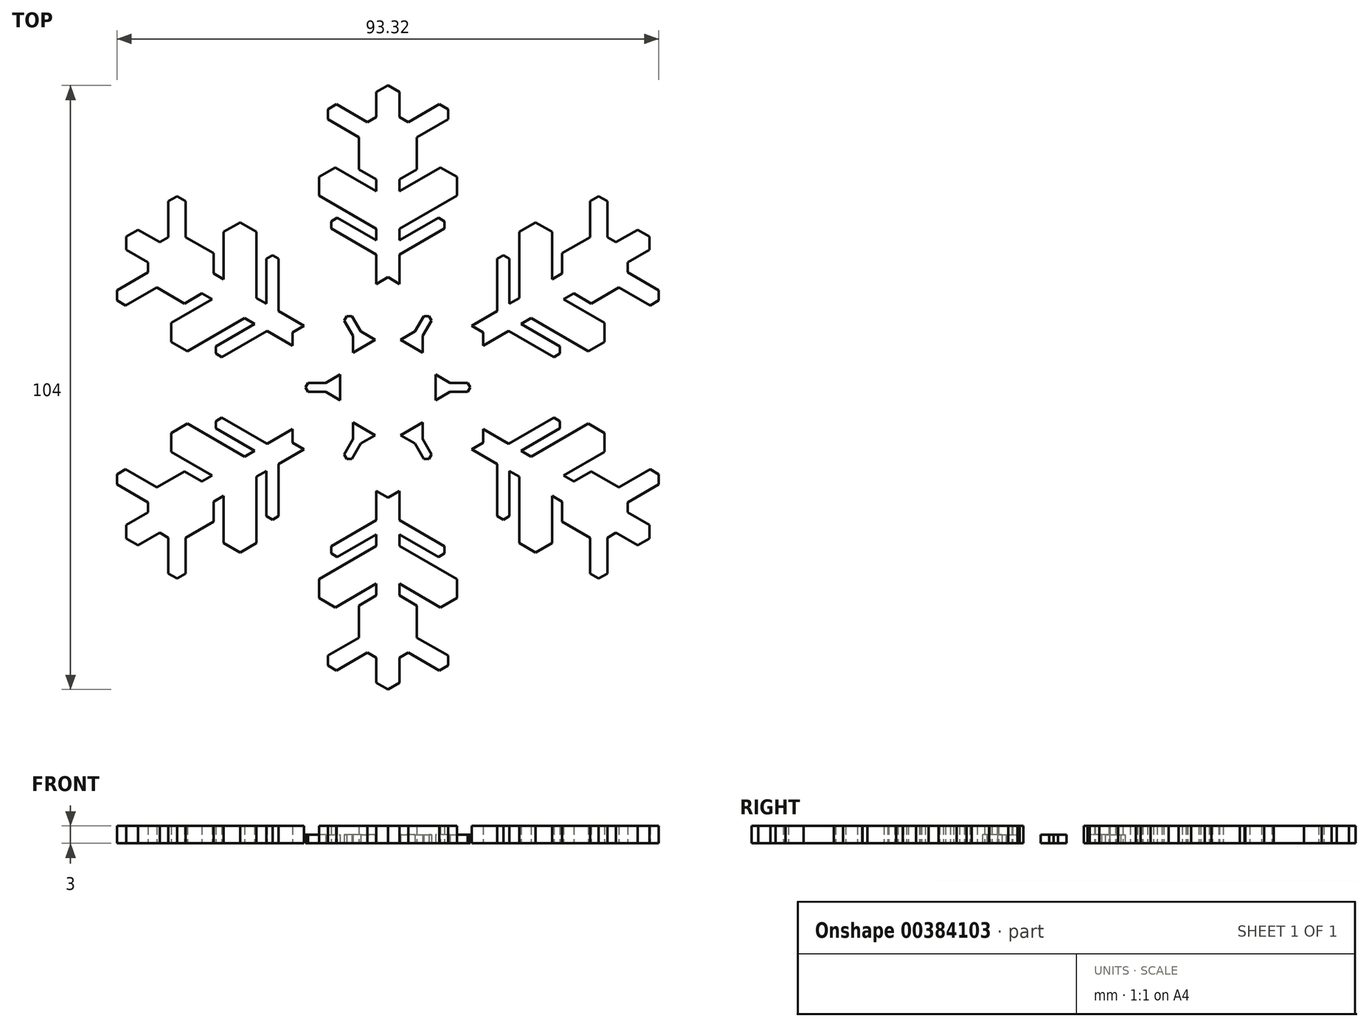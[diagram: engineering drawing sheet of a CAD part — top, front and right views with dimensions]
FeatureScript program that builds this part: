
annotation { "Feature Type Name" : "Feature", "Feature Type Description" : "" }
export const myFeature = defineFeature(function(context is Context, id is Id, definition is map)
    precondition{}
    {
        {
            var Q0;
            Q0=qCreatedBy(makeId("Top.planeOp"),FACE);
            var sketch = newSketch(context, id + "F0", { "sketchPlane" : qUnion([Q0])});
            skLineSegment(sketch, "E0", {"start": v(0, 26) * mm, "end": v(0, -26) * mm, "construction": true});
            skLineSegment(sketch, "E1", {"start": v(22.52, -13) * mm, "end": v(-22.52, 13) * mm, "construction": true});
            skLineSegment(sketch, "E2", {"start": v(22.52, 13) * mm, "end": v(-22.52, -13) * mm, "construction": true});
            skLineSegment(sketch, "E3", {"start": v(0, 9.48) * mm, "end": v(-8.21, 4.74) * mm});
            skLineSegment(sketch, "E4", {"start": v(0, 0) * mm, "end": v(-4.1, 7.11) * mm, "construction": true});
            skLineSegment(sketch, "E5", {"start": v(0, 0) * mm, "end": v(-3.22, 7.62) * mm});
            skLineSegment(sketch, "E6", {"start": v(0, 0) * mm, "end": v(-5, 6.6) * mm});
            skLineSegment(sketch, "E7", {"start": v(0, 2.4) * mm, "end": v(-2.08, 1.2) * mm});
            skLineSegment(sketch, "E8", {"start": v(-1, 8.9) * mm, "end": v(-1, 25.42) * mm});
            skLineSegment(sketch, "E9", {"start": v(-1, 25.42) * mm, "end": v(0, 26) * mm});
            skLineSegment(sketch, "E10", {"start": v(-1, 23.27) * mm, "end": v(-2.5, 22.4) * mm});
            skLineSegment(sketch, "E11", {"start": v(-2.5, 22.4) * mm, "end": v(-2.5, 18.78) * mm});
            skLineSegment(sketch, "E12", {"start": v(-2.5, 18.78) * mm, "end": v(-1, 17.91) * mm});
            skLineSegment(sketch, "E13", {"start": v(-1.75, 22.84) * mm, "end": v(-4.43, 24.38) * mm});
            skLineSegment(sketch, "E14", {"start": v(-4.43, 24.38) * mm, "end": v(-5.18, 23.95) * mm});
            skLineSegment(sketch, "E15", {"start": v(-5.18, 23.95) * mm, "end": v(-5.18, 23.08) * mm});
            skLineSegment(sketch, "E16", {"start": v(-5.18, 23.08) * mm, "end": v(-2.5, 21.54) * mm});
            skLineSegment(sketch, "E17", {"start": v(-5.18, 23.08) * mm, "end": v(-4.43, 24.38) * mm, "construction": true});
            skLineSegment(sketch, "E18", {"start": v(-5.18, 23.95) * mm, "end": v(-4.8, 23.73) * mm, "construction": true});
            skLineSegment(sketch, "E19", {"start": v(-4.8, 23.73) * mm, "end": v(-2.5, 22.4) * mm, "construction": true});
            skLineSegment(sketch, "E20", {"start": v(-1, 16.9) * mm, "end": v(-4.53, 18.94) * mm});
            skLineSegment(sketch, "E21", {"start": v(-4.53, 18.94) * mm, "end": v(-5.94, 18.13) * mm});
            skLineSegment(sketch, "E22", {"start": v(-5.94, 18.13) * mm, "end": v(-5.94, 16.5) * mm});
            skLineSegment(sketch, "E23", {"start": v(-5.94, 16.5) * mm, "end": v(-1, 13.65) * mm});
            skLineSegment(sketch, "E24", {"start": v(-5.94, 16.5) * mm, "end": v(-4.53, 18.94) * mm, "construction": true});
            skLineSegment(sketch, "E25", {"start": v(-5.94, 18.13) * mm, "end": v(-5.23, 17.72) * mm, "construction": true});
            skPoint(sketch, "E25.endSnap0", {"position": v(-5.23, 17.72) * mm});
            skLineSegment(sketch, "E26", {"start": v(-1, 12.67) * mm, "end": v(-4.35, 14.6) * mm});
            skLineSegment(sketch, "E27", {"start": v(-4.35, 14.6) * mm, "end": v(-4.89, 14.3) * mm});
            skLineSegment(sketch, "E28", {"start": v(-4.89, 14.3) * mm, "end": v(-4.89, 13.68) * mm});
            skLineSegment(sketch, "E29", {"start": v(-4.89, 13.68) * mm, "end": v(-1, 11.44) * mm});
            skLineSegment(sketch, "E30", {"start": v(-4.89, 13.68) * mm, "end": v(-4.35, 14.6) * mm, "construction": true});
            skLineSegment(sketch, "E31", {"start": v(-4.89, 14.3) * mm, "end": v(-4.62, 14.14) * mm, "construction": true});
            skLineSegment(sketch, "E32", {"start": v(-4.1, 7.11) * mm, "end": v(-15.85, 27.45) * mm, "construction": true});
            skLineSegment(sketch, "E33", {"start": v(-6.02, 10.43) * mm, "end": v(-2.2, 8.22) * mm});
            skLineSegment(sketch, "E34", {"start": v(-4.69, 9.66) * mm, "end": v(-6.2, 12.29) * mm});
            skLineSegment(sketch, "E35", {"start": v(-6.2, 12.29) * mm, "end": v(-7.1, 12.29) * mm});
            skLineSegment(sketch, "E36", {"start": v(-7.21, 4.16) * mm, "end": v(0, 8.33) * mm});
            skLineSegment(sketch, "E37.MirrorCS", {"start": v(5.18, 23.95) * mm, "end": v(4.8, 23.73) * mm, "construction": true});
            skLineSegment(sketch, "E38.MirrorCS", {"start": v(4.89, 14.3) * mm, "end": v(4.62, 14.14) * mm, "construction": true});
            skLineSegment(sketch, "E39.MirrorCS", {"start": v(4.43, 24.38) * mm, "end": v(5.18, 23.95) * mm});
            skLineSegment(sketch, "E40.MirrorCS", {"start": v(5.18, 23.95) * mm, "end": v(5.18, 23.08) * mm});
            skLineSegment(sketch, "E41.MirrorCS", {"start": v(5.94, 18.13) * mm, "end": v(5.94, 16.5) * mm});
            skLineSegment(sketch, "E42.MirrorCS", {"start": v(5.94, 18.13) * mm, "end": v(5.23, 17.72) * mm, "construction": true});
            skLineSegment(sketch, "E43.MirrorCS", {"start": v(4.89, 14.3) * mm, "end": v(4.89, 13.68) * mm});
            skLineSegment(sketch, "E44.MirrorCS", {"start": v(4.53, 18.94) * mm, "end": v(5.94, 18.13) * mm});
            skLineSegment(sketch, "E45.MirrorCS", {"start": v(4.89, 13.68) * mm, "end": v(4.35, 14.6) * mm, "construction": true});
            skLineSegment(sketch, "E46.MirrorCS", {"start": v(5.18, 23.08) * mm, "end": v(4.43, 24.38) * mm, "construction": true});
            skLineSegment(sketch, "E47.MirrorCS", {"start": v(4.35, 14.6) * mm, "end": v(4.89, 14.3) * mm});
            skLineSegment(sketch, "E48.MirrorCS", {"start": v(5.94, 16.5) * mm, "end": v(4.53, 18.94) * mm, "construction": true});
            skLineSegment(sketch, "E49.MirrorCS", {"start": v(1, 25.42) * mm, "end": v(0, 26) * mm});
            skLineSegment(sketch, "E50.MirrorCS", {"start": v(6.2, 12.29) * mm, "end": v(7.1, 12.29) * mm});
            skLineSegment(sketch, "E51.MirrorCS", {"start": v(1.75, 22.84) * mm, "end": v(4.43, 24.38) * mm});
            skLineSegment(sketch, "E52.MirrorCS", {"start": v(1, 23.27) * mm, "end": v(2.5, 22.4) * mm});
            skLineSegment(sketch, "E53.MirrorCS", {"start": v(1, 12.67) * mm, "end": v(4.35, 14.6) * mm});
            skLineSegment(sketch, "E54.MirrorCS", {"start": v(2.5, 18.78) * mm, "end": v(1, 17.91) * mm});
            skLineSegment(sketch, "E55.MirrorCS", {"start": v(4.69, 9.66) * mm, "end": v(6.2, 12.29) * mm});
            skPoint(sketch, "E56.MirrorP", {"position": v(5.23, 17.72) * mm});
            skLineSegment(sketch, "E57.MirrorCS", {"start": v(5.18, 23.08) * mm, "end": v(2.5, 21.54) * mm});
            skLineSegment(sketch, "E58.MirrorCS", {"start": v(4.89, 13.68) * mm, "end": v(1, 11.44) * mm});
            skLineSegment(sketch, "E59.MirrorCS", {"start": v(7.21, 4.16) * mm, "end": v(0, 8.33) * mm});
            skLineSegment(sketch, "E60.MirrorCS", {"start": v(5.94, 16.5) * mm, "end": v(1, 13.65) * mm});
            skLineSegment(sketch, "E61.MirrorCS", {"start": v(1, 16.9) * mm, "end": v(4.53, 18.94) * mm});
            skLineSegment(sketch, "E62.MirrorCS", {"start": v(2.5, 22.4) * mm, "end": v(2.5, 18.78) * mm});
            skLineSegment(sketch, "E63.MirrorCS", {"start": v(0, 9.48) * mm, "end": v(8.21, 4.74) * mm});
            skLineSegment(sketch, "E64.MirrorCS", {"start": v(0, 0) * mm, "end": v(4.1, 7.11) * mm, "construction": true});
            skLineSegment(sketch, "E65.MirrorCS", {"start": v(4.8, 23.73) * mm, "end": v(2.5, 22.4) * mm, "construction": true});
            skLineSegment(sketch, "E66.MirrorCS", {"start": v(6.02, 10.43) * mm, "end": v(2.2, 8.22) * mm});
            skLineSegment(sketch, "E67.MirrorCS", {"start": v(0, 0) * mm, "end": v(5, 6.6) * mm});
            skLineSegment(sketch, "E68.MirrorCS", {"start": v(0, 0) * mm, "end": v(3.22, 7.62) * mm});
            skLineSegment(sketch, "E69.MirrorCS", {"start": v(1, 8.9) * mm, "end": v(1, 25.42) * mm});
            skLineSegment(sketch, "E70.MirrorCS", {"start": v(0, 2.4) * mm, "end": v(2.08, 1.2) * mm});
            skLineSegment(sketch, "E71.1.0", {"start": v(0, 8.33) * mm, "end": v(-7.21, 4.16) * mm});
            skLineSegment(sketch, "E71.1.1", {"start": v(-15.14, 7.58) * mm, "end": v(-18.67, 5.55) * mm});
            skLineSegment(sketch, "E71.1.2", {"start": v(-7.21, 5.32) * mm, "end": v(-21.52, 13.58) * mm});
            skLineSegment(sketch, "E71.1.3", {"start": v(-18.15, 13.37) * mm, "end": v(-15.01, 11.56) * mm});
            skLineSegment(sketch, "E71.1.4", {"start": v(-14.29, 2.6) * mm, "end": v(-10.4, 4.85) * mm});
            skPoint(sketch, "E71.1.5", {"position": v(-12.73, 13.4) * mm});
            skLineSegment(sketch, "E71.1.6", {"start": v(-22.95, 7.7) * mm, "end": v(-20.65, 9.04) * mm, "construction": true});
            skLineSegment(sketch, "E71.1.7", {"start": v(-11.32, 13.4) * mm, "end": v(-11.32, 7.7) * mm});
            skLineSegment(sketch, "E71.1.8", {"start": v(-7.21, -4.16) * mm, "end": v(-7.21, 4.16) * mm});
            skLineSegment(sketch, "E71.1.9", {"start": v(-14.14, 9.32) * mm, "end": v(-14.14, 13.4) * mm});
            skLineSegment(sketch, "E71.1.11", {"start": v(-2.08, 1.2) * mm, "end": v(0, 2.4) * mm});
            skLineSegment(sketch, "E71.1.13", {"start": v(-8.21, 4.74) * mm, "end": v(0, 9.48) * mm});
            skLineSegment(sketch, "E71.1.14", {"start": v(-18.9, 12.93) * mm, "end": v(-18.9, 16.02) * mm});
            skPoint(sketch, "E71.1.15", {"position": v(-17.96, 4.33) * mm});
            skLineSegment(sketch, "E71.1.16", {"start": v(-15.01, 11.56) * mm, "end": v(-15.01, 9.82) * mm});
            skLineSegment(sketch, "E71.1.17", {"start": v(-8.21, 4.74) * mm, "end": v(-8.21, -4.74) * mm});
            skLineSegment(sketch, "E71.1.18", {"start": v(0, 0) * mm, "end": v(-8.21, 0) * mm, "construction": true});
            skLineSegment(sketch, "E71.1.19", {"start": v(0, 0) * mm, "end": v(-8.21, 1.02) * mm});
            skLineSegment(sketch, "E71.1.20", {"start": v(0, 0) * mm, "end": v(-8.21, -1.02) * mm});
            skLineSegment(sketch, "E71.1.21", {"start": v(-2.08, 1.2) * mm, "end": v(-2.08, -1.2) * mm});
            skLineSegment(sketch, "E71.1.22", {"start": v(-8.21, 3.59) * mm, "end": v(-22.52, 11.85) * mm});
            skLineSegment(sketch, "E71.1.23", {"start": v(-20.65, 9.04) * mm, "end": v(-17.51, 7.23) * mm});
            skLineSegment(sketch, "E71.1.24", {"start": v(-17.51, 7.23) * mm, "end": v(-16.01, 8.1) * mm});
            skLineSegment(sketch, "E71.1.25", {"start": v(-6.02, 8.89) * mm, "end": v(-7.54, 11.52) * mm});
            skLineSegment(sketch, "E71.1.26", {"start": v(-17.26, 3.1) * mm, "end": v(-12.32, 5.96) * mm});
            skLineSegment(sketch, "E71.1.27", {"start": v(-22.58, 7.06) * mm, "end": v(-19.9, 8.6) * mm});
            skLineSegment(sketch, "E71.1.28", {"start": v(-18.15, 16.02) * mm, "end": v(-18.15, 13.37) * mm, "construction": true});
            skLineSegment(sketch, "E71.1.29", {"start": v(-17.4, 16.02) * mm, "end": v(-17.4, 12.93) * mm});
            skLineSegment(sketch, "E71.1.30", {"start": v(-6.02, 10.43) * mm, "end": v(-6.02, 6) * mm});
            skLineSegment(sketch, "E71.1.31", {"start": v(-12.04, 0) * mm, "end": v(-8.21, 2.2) * mm});
            skLineSegment(sketch, "E71.1.32", {"start": v(-9.4, 11.07) * mm, "end": v(-9.4, 6.58) * mm});
            skLineSegment(sketch, "E71.1.34", {"start": v(-10.7, 0.77) * mm, "end": v(-13.75, 0.77) * mm});
            skLineSegment(sketch, "E71.1.35", {"start": v(-19.65, 12.5) * mm, "end": v(-18.15, 13.37) * mm});
            skLineSegment(sketch, "E71.1.36", {"start": v(-20.65, 9.9) * mm, "end": v(-23.33, 8.36) * mm});
            skLineSegment(sketch, "E71.1.37", {"start": v(-10.47, 7.2) * mm, "end": v(-10.47, 11.07) * mm});
            skLineSegment(sketch, "E71.1.38", {"start": v(-13.75, 0.77) * mm, "end": v(-14.2, 0) * mm});
            skLineSegment(sketch, "E71.1.39", {"start": v(-20.65, 10.77) * mm, "end": v(-20.65, 9.04) * mm});
            skLineSegment(sketch, "E71.1.40", {"start": v(-7.54, 11.52) * mm, "end": v(-7.1, 12.29) * mm});
            skLineSegment(sketch, "E71.1.41", {"start": v(-11.47, 5.47) * mm, "end": v(-14.82, 3.53) * mm});
            skLineSegment(sketch, "E71.1.42", {"start": v(-22.52, 11.85) * mm, "end": v(-22.52, 13) * mm});
            skLineSegment(sketch, "E71.1.43", {"start": v(-11.32, 13.4) * mm, "end": v(-14.14, 13.4) * mm, "construction": true});
            skLineSegment(sketch, "E71.1.44", {"start": v(-17.26, 3.1) * mm, "end": v(-18.67, 5.55) * mm, "construction": true});
            skLineSegment(sketch, "E71.1.45", {"start": v(-21.52, 13.58) * mm, "end": v(-22.52, 13) * mm});
            skLineSegment(sketch, "E71.1.46", {"start": v(-9.94, 11.38) * mm, "end": v(-9.4, 11.07) * mm});
            skLineSegment(sketch, "E71.1.47", {"start": v(-12.73, 14.2) * mm, "end": v(-12.73, 13.4) * mm, "construction": true});
            skLineSegment(sketch, "E71.1.48", {"start": v(-23.33, 8.36) * mm, "end": v(-23.33, 7.5) * mm});
            skLineSegment(sketch, "E71.1.49", {"start": v(-9.4, 11.07) * mm, "end": v(-10.47, 11.07) * mm, "construction": true});
            skLineSegment(sketch, "E71.1.50", {"start": v(-14.82, 2.92) * mm, "end": v(-14.56, 3.07) * mm, "construction": true});
            skLineSegment(sketch, "E71.1.51", {"start": v(-14.82, 3.53) * mm, "end": v(-14.82, 2.92) * mm});
            skLineSegment(sketch, "E71.1.52", {"start": v(-14.82, 2.92) * mm, "end": v(-14.29, 2.6) * mm});
            skLineSegment(sketch, "E71.1.53", {"start": v(-14.14, 13.4) * mm, "end": v(-12.73, 14.2) * mm});
            skLineSegment(sketch, "E71.1.54", {"start": v(-18.67, 5.55) * mm, "end": v(-18.67, 3.92) * mm});
            skLineSegment(sketch, "E71.1.55", {"start": v(-18.67, 3.92) * mm, "end": v(-17.26, 3.1) * mm});
            skLineSegment(sketch, "E71.1.56", {"start": v(-9.94, 11.38) * mm, "end": v(-9.94, 11.07) * mm, "construction": true});
            skLineSegment(sketch, "E71.1.57", {"start": v(-18.15, 16.46) * mm, "end": v(-18.15, 16.02) * mm, "construction": true});
            skLineSegment(sketch, "E71.1.58", {"start": v(-17.4, 16.02) * mm, "end": v(-18.9, 16.02) * mm, "construction": true});
            skLineSegment(sketch, "E71.1.59", {"start": v(-23.33, 7.5) * mm, "end": v(-22.58, 7.06) * mm});
            skLineSegment(sketch, "E71.1.60", {"start": v(-14.29, 2.6) * mm, "end": v(-14.82, 3.53) * mm, "construction": true});
            skLineSegment(sketch, "E71.1.61", {"start": v(-10.47, 11.07) * mm, "end": v(-9.94, 11.38) * mm});
            skLineSegment(sketch, "E71.1.62", {"start": v(-18.9, 16.02) * mm, "end": v(-18.15, 16.46) * mm});
            skLineSegment(sketch, "E71.1.63", {"start": v(-18.15, 16.46) * mm, "end": v(-17.4, 16.02) * mm});
            skLineSegment(sketch, "E71.1.64", {"start": v(-22.58, 7.06) * mm, "end": v(-23.33, 8.36) * mm, "construction": true});
            skLineSegment(sketch, "E71.1.65", {"start": v(-12.73, 14.2) * mm, "end": v(-11.32, 13.4) * mm});
            skLineSegment(sketch, "E71.1.66", {"start": v(-18.67, 3.92) * mm, "end": v(-17.96, 4.33) * mm, "construction": true});
            skLineSegment(sketch, "E71.1.67", {"start": v(-23.33, 7.5) * mm, "end": v(-22.95, 7.7) * mm, "construction": true});
            skLineSegment(sketch, "E71.2.0", {"start": v(-7.21, 4.16) * mm, "end": v(-7.21, -4.16) * mm});
            skLineSegment(sketch, "E71.2.1", {"start": v(-14.14, -9.32) * mm, "end": v(-14.14, -13.4) * mm});
            skLineSegment(sketch, "E71.2.2", {"start": v(-8.21, -3.59) * mm, "end": v(-22.52, -11.85) * mm});
            skLineSegment(sketch, "E71.2.3", {"start": v(-20.65, -9.04) * mm, "end": v(-17.51, -7.23) * mm});
            skLineSegment(sketch, "E71.2.4", {"start": v(-9.4, -11.07) * mm, "end": v(-9.4, -6.58) * mm});
            skPoint(sketch, "E71.2.5", {"position": v(-17.96, -4.33) * mm});
            skLineSegment(sketch, "E71.2.6", {"start": v(-18.15, -16.02) * mm, "end": v(-18.15, -13.37) * mm, "construction": true});
            skLineSegment(sketch, "E71.2.7", {"start": v(-17.26, -3.1) * mm, "end": v(-12.32, -5.96) * mm});
            skLineSegment(sketch, "E71.2.8", {"start": v(0, -8.33) * mm, "end": v(-7.21, -4.16) * mm});
            skLineSegment(sketch, "E71.2.9", {"start": v(-15.14, -7.58) * mm, "end": v(-18.67, -5.55) * mm});
            skLineSegment(sketch, "E71.2.10", {"start": v(0, 0) * mm, "end": v(-8.21, -1.02) * mm});
            skLineSegment(sketch, "E71.2.11", {"start": v(-2.08, -1.2) * mm, "end": v(-2.08, 1.2) * mm});
            skLineSegment(sketch, "E71.2.12", {"start": v(0, 0) * mm, "end": v(-8.21, 0) * mm, "construction": true});
            skLineSegment(sketch, "E71.2.13", {"start": v(-8.21, -4.74) * mm, "end": v(-8.21, 4.74) * mm});
            skLineSegment(sketch, "E71.2.14", {"start": v(-20.65, -9.9) * mm, "end": v(-23.33, -8.36) * mm});
            skPoint(sketch, "E71.2.15", {"position": v(-12.73, -13.4) * mm});
            skLineSegment(sketch, "E71.2.16", {"start": v(-17.51, -7.23) * mm, "end": v(-16.01, -8.1) * mm});
            skLineSegment(sketch, "E71.2.17", {"start": v(-8.21, -4.74) * mm, "end": v(0, -9.48) * mm});
            skLineSegment(sketch, "E71.2.18", {"start": v(0, 0) * mm, "end": v(-4.1, -7.11) * mm, "construction": true});
            skLineSegment(sketch, "E71.2.19", {"start": v(0, 0) * mm, "end": v(-5, -6.6) * mm});
            skLineSegment(sketch, "E71.2.20", {"start": v(0, 0) * mm, "end": v(-3.22, -7.62) * mm});
            skLineSegment(sketch, "E71.2.21", {"start": v(-2.08, -1.2) * mm, "end": v(0, -2.4) * mm});
            skLineSegment(sketch, "E71.2.22", {"start": v(-7.21, -5.32) * mm, "end": v(-21.52, -13.58) * mm});
            skLineSegment(sketch, "E71.2.23", {"start": v(-18.15, -13.37) * mm, "end": v(-15.01, -11.56) * mm});
            skLineSegment(sketch, "E71.2.24", {"start": v(-15.01, -11.56) * mm, "end": v(-15.01, -9.82) * mm});
            skLineSegment(sketch, "E71.2.25", {"start": v(-10.7, -0.77) * mm, "end": v(-13.75, -0.77) * mm});
            skLineSegment(sketch, "E71.2.26", {"start": v(-11.32, -13.4) * mm, "end": v(-11.32, -7.7) * mm});
            skLineSegment(sketch, "E71.2.27", {"start": v(-17.4, -16.02) * mm, "end": v(-17.4, -12.93) * mm});
            skLineSegment(sketch, "E71.2.28", {"start": v(-22.95, -7.7) * mm, "end": v(-20.65, -9.04) * mm, "construction": true});
            skLineSegment(sketch, "E71.2.29", {"start": v(-22.58, -7.06) * mm, "end": v(-19.9, -8.6) * mm});
            skLineSegment(sketch, "E71.2.30", {"start": v(-12.04, 0) * mm, "end": v(-8.21, -2.2) * mm});
            skLineSegment(sketch, "E71.2.31", {"start": v(-6.02, -10.43) * mm, "end": v(-6.02, -6) * mm});
            skLineSegment(sketch, "E71.2.32", {"start": v(-14.29, -2.6) * mm, "end": v(-10.4, -4.85) * mm});
            skLineSegment(sketch, "E71.2.33", {"start": v(0, 0) * mm, "end": v(-8.21, 1.02) * mm});
            skLineSegment(sketch, "E71.2.34", {"start": v(-6.02, -8.89) * mm, "end": v(-7.54, -11.52) * mm});
            skLineSegment(sketch, "E71.2.35", {"start": v(-20.65, -10.77) * mm, "end": v(-20.65, -9.04) * mm});
            skLineSegment(sketch, "E71.2.36", {"start": v(-18.9, -12.93) * mm, "end": v(-18.9, -16.02) * mm});
            skLineSegment(sketch, "E71.2.37", {"start": v(-11.47, -5.47) * mm, "end": v(-14.82, -3.53) * mm});
            skLineSegment(sketch, "E71.2.38", {"start": v(-7.54, -11.52) * mm, "end": v(-7.1, -12.29) * mm});
            skLineSegment(sketch, "E71.2.39", {"start": v(-19.65, -12.5) * mm, "end": v(-18.15, -13.37) * mm});
            skLineSegment(sketch, "E71.2.40", {"start": v(-13.75, -0.77) * mm, "end": v(-14.2, 0) * mm});
            skLineSegment(sketch, "E71.2.41", {"start": v(-10.47, -7.2) * mm, "end": v(-10.47, -11.07) * mm});
            skLineSegment(sketch, "E71.2.42", {"start": v(-21.52, -13.58) * mm, "end": v(-22.52, -13) * mm});
            skLineSegment(sketch, "E71.2.43", {"start": v(-17.26, -3.1) * mm, "end": v(-18.67, -5.55) * mm, "construction": true});
            skLineSegment(sketch, "E71.2.44", {"start": v(-11.32, -13.4) * mm, "end": v(-14.14, -13.4) * mm, "construction": true});
            skLineSegment(sketch, "E71.2.45", {"start": v(-22.52, -11.85) * mm, "end": v(-22.52, -13) * mm});
            skLineSegment(sketch, "E71.2.46", {"start": v(-14.82, -2.92) * mm, "end": v(-14.29, -2.6) * mm});
            skLineSegment(sketch, "E71.2.47", {"start": v(-18.67, -3.92) * mm, "end": v(-17.96, -4.33) * mm, "construction": true});
            skLineSegment(sketch, "E71.2.48", {"start": v(-18.9, -16.02) * mm, "end": v(-18.15, -16.46) * mm});
            skLineSegment(sketch, "E71.2.49", {"start": v(-14.29, -2.6) * mm, "end": v(-14.82, -3.53) * mm, "construction": true});
            skLineSegment(sketch, "E71.2.50", {"start": v(-9.94, -11.38) * mm, "end": v(-9.94, -11.07) * mm, "construction": true});
            skLineSegment(sketch, "E71.2.51", {"start": v(-10.47, -11.07) * mm, "end": v(-9.94, -11.38) * mm});
            skLineSegment(sketch, "E71.2.52", {"start": v(-9.94, -11.38) * mm, "end": v(-9.4, -11.07) * mm});
            skLineSegment(sketch, "E71.2.53", {"start": v(-18.67, -5.55) * mm, "end": v(-18.67, -3.92) * mm});
            skLineSegment(sketch, "E71.2.54", {"start": v(-14.14, -13.4) * mm, "end": v(-12.73, -14.2) * mm});
            skLineSegment(sketch, "E71.2.55", {"start": v(-12.73, -14.2) * mm, "end": v(-11.32, -13.4) * mm});
            skLineSegment(sketch, "E71.2.56", {"start": v(-14.82, -2.92) * mm, "end": v(-14.56, -3.07) * mm, "construction": true});
            skLineSegment(sketch, "E71.2.57", {"start": v(-23.33, -7.5) * mm, "end": v(-22.95, -7.7) * mm, "construction": true});
            skLineSegment(sketch, "E71.2.58", {"start": v(-22.58, -7.06) * mm, "end": v(-23.33, -8.36) * mm, "construction": true});
            skLineSegment(sketch, "E71.2.59", {"start": v(-18.15, -16.46) * mm, "end": v(-17.4, -16.02) * mm});
            skLineSegment(sketch, "E71.2.60", {"start": v(-9.4, -11.07) * mm, "end": v(-10.47, -11.07) * mm, "construction": true});
            skLineSegment(sketch, "E71.2.61", {"start": v(-14.82, -3.53) * mm, "end": v(-14.82, -2.92) * mm});
            skLineSegment(sketch, "E71.2.62", {"start": v(-23.33, -8.36) * mm, "end": v(-23.33, -7.5) * mm});
            skLineSegment(sketch, "E71.2.63", {"start": v(-23.33, -7.5) * mm, "end": v(-22.58, -7.06) * mm});
            skLineSegment(sketch, "E71.2.64", {"start": v(-17.4, -16.02) * mm, "end": v(-18.9, -16.02) * mm, "construction": true});
            skLineSegment(sketch, "E71.2.65", {"start": v(-18.67, -3.92) * mm, "end": v(-17.26, -3.1) * mm});
            skLineSegment(sketch, "E71.2.66", {"start": v(-12.73, -14.2) * mm, "end": v(-12.73, -13.4) * mm, "construction": true});
            skLineSegment(sketch, "E71.2.67", {"start": v(-18.15, -16.46) * mm, "end": v(-18.15, -16.02) * mm, "construction": true});
            skLineSegment(sketch, "E71.3.0", {"start": v(-7.21, -4.16) * mm, "end": v(0, -8.33) * mm});
            skLineSegment(sketch, "E71.3.1", {"start": v(1, -16.9) * mm, "end": v(4.53, -18.94) * mm});
            skLineSegment(sketch, "E71.3.2", {"start": v(-1, -8.9) * mm, "end": v(-1, -25.42) * mm});
            skLineSegment(sketch, "E71.3.3", {"start": v(-2.5, -22.4) * mm, "end": v(-2.5, -18.78) * mm});
            skLineSegment(sketch, "E71.3.4", {"start": v(4.89, -13.68) * mm, "end": v(1, -11.44) * mm});
            skPoint(sketch, "E71.3.5", {"position": v(-5.23, -17.72) * mm});
            skLineSegment(sketch, "E71.3.6", {"start": v(4.8, -23.73) * mm, "end": v(2.5, -22.4) * mm, "construction": true});
            skLineSegment(sketch, "E71.3.7", {"start": v(-5.94, -16.5) * mm, "end": v(-1, -13.65) * mm});
            skLineSegment(sketch, "E71.3.8", {"start": v(7.21, -4.16) * mm, "end": v(0, -8.33) * mm});
            skLineSegment(sketch, "E71.3.9", {"start": v(-1, -16.9) * mm, "end": v(-4.53, -18.94) * mm});
            skLineSegment(sketch, "E71.3.10", {"start": v(0, 0) * mm, "end": v(-3.22, -7.62) * mm});
            skLineSegment(sketch, "E71.3.11", {"start": v(0, -2.4) * mm, "end": v(-2.08, -1.2) * mm});
            skLineSegment(sketch, "E71.3.12", {"start": v(0, 0) * mm, "end": v(-4.1, -7.11) * mm, "construction": true});
            skLineSegment(sketch, "E71.3.13", {"start": v(0, -9.48) * mm, "end": v(-8.21, -4.74) * mm});
            skLineSegment(sketch, "E71.3.14", {"start": v(-1.75, -22.84) * mm, "end": v(-4.43, -24.38) * mm});
            skPoint(sketch, "E71.3.15", {"position": v(5.23, -17.72) * mm});
            skLineSegment(sketch, "E71.3.16", {"start": v(-2.5, -18.78) * mm, "end": v(-1, -17.91) * mm});
            skLineSegment(sketch, "E71.3.17", {"start": v(0, -9.48) * mm, "end": v(8.21, -4.74) * mm});
            skLineSegment(sketch, "E71.3.18", {"start": v(0, 0) * mm, "end": v(4.1, -7.11) * mm, "construction": true});
            skLineSegment(sketch, "E71.3.19", {"start": v(0, 0) * mm, "end": v(3.22, -7.62) * mm});
            skLineSegment(sketch, "E71.3.20", {"start": v(0, 0) * mm, "end": v(5, -6.6) * mm});
            skLineSegment(sketch, "E71.3.21", {"start": v(0, -2.4) * mm, "end": v(2.08, -1.2) * mm});
            skLineSegment(sketch, "E71.3.22", {"start": v(1, -8.9) * mm, "end": v(1, -25.42) * mm});
            skLineSegment(sketch, "E71.3.23", {"start": v(2.5, -22.4) * mm, "end": v(2.5, -18.78) * mm});
            skLineSegment(sketch, "E71.3.24", {"start": v(2.5, -18.78) * mm, "end": v(1, -17.91) * mm});
            skLineSegment(sketch, "E71.3.25", {"start": v(-4.69, -9.66) * mm, "end": v(-6.2, -12.29) * mm});
            skLineSegment(sketch, "E71.3.26", {"start": v(5.94, -16.5) * mm, "end": v(1, -13.65) * mm});
            skLineSegment(sketch, "E71.3.27", {"start": v(5.18, -23.08) * mm, "end": v(2.5, -21.54) * mm});
            skLineSegment(sketch, "E71.3.28", {"start": v(-4.8, -23.73) * mm, "end": v(-2.5, -22.4) * mm, "construction": true});
            skLineSegment(sketch, "E71.3.29", {"start": v(-5.18, -23.08) * mm, "end": v(-2.5, -21.54) * mm});
            skLineSegment(sketch, "E71.3.30", {"start": v(-6.02, -10.43) * mm, "end": v(-2.2, -8.22) * mm});
            skLineSegment(sketch, "E71.3.31", {"start": v(6.02, -10.43) * mm, "end": v(2.2, -8.22) * mm});
            skLineSegment(sketch, "E71.3.32", {"start": v(-4.89, -13.68) * mm, "end": v(-1, -11.44) * mm});
            skLineSegment(sketch, "E71.3.33", {"start": v(0, 0) * mm, "end": v(-5, -6.6) * mm});
            skLineSegment(sketch, "E71.3.34", {"start": v(4.69, -9.66) * mm, "end": v(6.2, -12.29) * mm});
            skLineSegment(sketch, "E71.3.35", {"start": v(-1, -23.27) * mm, "end": v(-2.5, -22.4) * mm});
            skLineSegment(sketch, "E71.3.36", {"start": v(1.75, -22.84) * mm, "end": v(4.43, -24.38) * mm});
            skLineSegment(sketch, "E71.3.37", {"start": v(-1, -12.67) * mm, "end": v(-4.35, -14.6) * mm});
            skLineSegment(sketch, "E71.3.38", {"start": v(6.2, -12.29) * mm, "end": v(7.1, -12.29) * mm});
            skLineSegment(sketch, "E71.3.39", {"start": v(1, -23.27) * mm, "end": v(2.5, -22.4) * mm});
            skLineSegment(sketch, "E71.3.40", {"start": v(-6.2, -12.29) * mm, "end": v(-7.1, -12.29) * mm});
            skLineSegment(sketch, "E71.3.41", {"start": v(1, -12.67) * mm, "end": v(4.35, -14.6) * mm});
            skLineSegment(sketch, "E71.3.42", {"start": v(1, -25.42) * mm, "end": v(0, -26) * mm});
            skLineSegment(sketch, "E71.3.43", {"start": v(-5.94, -16.5) * mm, "end": v(-4.53, -18.94) * mm, "construction": true});
            skLineSegment(sketch, "E71.3.44", {"start": v(5.94, -16.5) * mm, "end": v(4.53, -18.94) * mm, "construction": true});
            skLineSegment(sketch, "E71.3.45", {"start": v(-1, -25.42) * mm, "end": v(0, -26) * mm});
            skLineSegment(sketch, "E71.3.46", {"start": v(-4.89, -14.3) * mm, "end": v(-4.89, -13.68) * mm});
            skLineSegment(sketch, "E71.3.47", {"start": v(-5.94, -18.13) * mm, "end": v(-5.23, -17.72) * mm, "construction": true});
            skLineSegment(sketch, "E71.3.48", {"start": v(4.43, -24.38) * mm, "end": v(5.18, -23.95) * mm});
            skLineSegment(sketch, "E71.3.49", {"start": v(-4.89, -13.68) * mm, "end": v(-4.35, -14.6) * mm, "construction": true});
            skLineSegment(sketch, "E71.3.50", {"start": v(4.89, -14.3) * mm, "end": v(4.62, -14.14) * mm, "construction": true});
            skLineSegment(sketch, "E71.3.51", {"start": v(4.35, -14.6) * mm, "end": v(4.89, -14.3) * mm});
            skLineSegment(sketch, "E71.3.52", {"start": v(4.89, -14.3) * mm, "end": v(4.89, -13.68) * mm});
            skLineSegment(sketch, "E71.3.53", {"start": v(-4.53, -18.94) * mm, "end": v(-5.94, -18.13) * mm});
            skLineSegment(sketch, "E71.3.54", {"start": v(4.53, -18.94) * mm, "end": v(5.94, -18.13) * mm});
            skLineSegment(sketch, "E71.3.55", {"start": v(5.94, -18.13) * mm, "end": v(5.94, -16.5) * mm});
            skLineSegment(sketch, "E71.3.56", {"start": v(-4.89, -14.3) * mm, "end": v(-4.62, -14.14) * mm, "construction": true});
            skLineSegment(sketch, "E71.3.57", {"start": v(-5.18, -23.95) * mm, "end": v(-4.8, -23.73) * mm, "construction": true});
            skLineSegment(sketch, "E71.3.58", {"start": v(-5.18, -23.08) * mm, "end": v(-4.43, -24.38) * mm, "construction": true});
            skLineSegment(sketch, "E71.3.59", {"start": v(5.18, -23.95) * mm, "end": v(5.18, -23.08) * mm});
            skLineSegment(sketch, "E71.3.60", {"start": v(4.89, -13.68) * mm, "end": v(4.35, -14.6) * mm, "construction": true});
            skLineSegment(sketch, "E71.3.61", {"start": v(-4.35, -14.6) * mm, "end": v(-4.89, -14.3) * mm});
            skLineSegment(sketch, "E71.3.62", {"start": v(-4.43, -24.38) * mm, "end": v(-5.18, -23.95) * mm});
            skLineSegment(sketch, "E71.3.63", {"start": v(-5.18, -23.95) * mm, "end": v(-5.18, -23.08) * mm});
            skLineSegment(sketch, "E71.3.64", {"start": v(5.18, -23.08) * mm, "end": v(4.43, -24.38) * mm, "construction": true});
            skLineSegment(sketch, "E71.3.65", {"start": v(-5.94, -18.13) * mm, "end": v(-5.94, -16.5) * mm});
            skLineSegment(sketch, "E71.3.66", {"start": v(5.94, -18.13) * mm, "end": v(5.23, -17.72) * mm, "construction": true});
            skLineSegment(sketch, "E71.3.67", {"start": v(5.18, -23.95) * mm, "end": v(4.8, -23.73) * mm, "construction": true});
            skLineSegment(sketch, "E71.4.0", {"start": v(0, -8.33) * mm, "end": v(7.21, -4.16) * mm});
            skLineSegment(sketch, "E71.4.1", {"start": v(15.14, -7.58) * mm, "end": v(18.67, -5.55) * mm});
            skLineSegment(sketch, "E71.4.2", {"start": v(7.21, -5.32) * mm, "end": v(21.52, -13.58) * mm});
            skLineSegment(sketch, "E71.4.3", {"start": v(18.15, -13.37) * mm, "end": v(15.01, -11.56) * mm});
            skLineSegment(sketch, "E71.4.4", {"start": v(14.29, -2.6) * mm, "end": v(10.4, -4.85) * mm});
            skPoint(sketch, "E71.4.5", {"position": v(12.73, -13.4) * mm});
            skLineSegment(sketch, "E71.4.6", {"start": v(22.95, -7.7) * mm, "end": v(20.65, -9.04) * mm, "construction": true});
            skLineSegment(sketch, "E71.4.7", {"start": v(11.32, -13.4) * mm, "end": v(11.32, -7.7) * mm});
            skLineSegment(sketch, "E71.4.8", {"start": v(7.21, 4.16) * mm, "end": v(7.21, -4.16) * mm});
            skLineSegment(sketch, "E71.4.9", {"start": v(14.14, -9.32) * mm, "end": v(14.14, -13.4) * mm});
            skLineSegment(sketch, "E71.4.10", {"start": v(0, 0) * mm, "end": v(5, -6.6) * mm});
            skLineSegment(sketch, "E71.4.11", {"start": v(2.08, -1.2) * mm, "end": v(0, -2.4) * mm});
            skLineSegment(sketch, "E71.4.12", {"start": v(0, 0) * mm, "end": v(4.1, -7.11) * mm, "construction": true});
            skLineSegment(sketch, "E71.4.13", {"start": v(8.21, -4.74) * mm, "end": v(0, -9.48) * mm});
            skLineSegment(sketch, "E71.4.14", {"start": v(18.9, -12.93) * mm, "end": v(18.9, -16.02) * mm});
            skPoint(sketch, "E71.4.15", {"position": v(17.96, -4.33) * mm});
            skLineSegment(sketch, "E71.4.16", {"start": v(15.01, -11.56) * mm, "end": v(15.01, -9.82) * mm});
            skLineSegment(sketch, "E71.4.17", {"start": v(8.21, -4.74) * mm, "end": v(8.21, 4.74) * mm});
            skLineSegment(sketch, "E71.4.18", {"start": v(0, 0) * mm, "end": v(8.21, 0) * mm, "construction": true});
            skLineSegment(sketch, "E71.4.19", {"start": v(0, 0) * mm, "end": v(8.21, -1.02) * mm});
            skLineSegment(sketch, "E71.4.20", {"start": v(0, 0) * mm, "end": v(8.21, 1.02) * mm});
            skLineSegment(sketch, "E71.4.21", {"start": v(2.08, -1.2) * mm, "end": v(2.08, 1.2) * mm});
            skLineSegment(sketch, "E71.4.22", {"start": v(8.21, -3.59) * mm, "end": v(22.52, -11.85) * mm});
            skLineSegment(sketch, "E71.4.23", {"start": v(20.65, -9.04) * mm, "end": v(17.51, -7.23) * mm});
            skLineSegment(sketch, "E71.4.24", {"start": v(17.51, -7.23) * mm, "end": v(16.01, -8.1) * mm});
            skLineSegment(sketch, "E71.4.25", {"start": v(6.02, -8.89) * mm, "end": v(7.54, -11.52) * mm});
            skLineSegment(sketch, "E71.4.26", {"start": v(17.26, -3.1) * mm, "end": v(12.32, -5.96) * mm});
            skLineSegment(sketch, "E71.4.27", {"start": v(22.58, -7.06) * mm, "end": v(19.9, -8.6) * mm});
            skLineSegment(sketch, "E71.4.28", {"start": v(18.15, -16.02) * mm, "end": v(18.15, -13.37) * mm, "construction": true});
            skLineSegment(sketch, "E71.4.29", {"start": v(17.4, -16.02) * mm, "end": v(17.4, -12.93) * mm});
            skLineSegment(sketch, "E71.4.30", {"start": v(6.02, -10.43) * mm, "end": v(6.02, -6) * mm});
            skLineSegment(sketch, "E71.4.31", {"start": v(12.04, 0) * mm, "end": v(8.21, -2.2) * mm});
            skLineSegment(sketch, "E71.4.32", {"start": v(9.4, -11.07) * mm, "end": v(9.4, -6.58) * mm});
            skLineSegment(sketch, "E71.4.33", {"start": v(0, 0) * mm, "end": v(3.22, -7.62) * mm});
            skLineSegment(sketch, "E71.4.34", {"start": v(10.7, -0.77) * mm, "end": v(13.75, -0.77) * mm});
            skLineSegment(sketch, "E71.4.35", {"start": v(19.65, -12.5) * mm, "end": v(18.15, -13.37) * mm});
            skLineSegment(sketch, "E71.4.36", {"start": v(20.65, -9.9) * mm, "end": v(23.33, -8.36) * mm});
            skLineSegment(sketch, "E71.4.37", {"start": v(10.47, -7.2) * mm, "end": v(10.47, -11.07) * mm});
            skLineSegment(sketch, "E71.4.38", {"start": v(13.75, -0.77) * mm, "end": v(14.2, 0) * mm});
            skLineSegment(sketch, "E71.4.39", {"start": v(20.65, -10.77) * mm, "end": v(20.65, -9.04) * mm});
            skLineSegment(sketch, "E71.4.40", {"start": v(7.54, -11.52) * mm, "end": v(7.1, -12.29) * mm});
            skLineSegment(sketch, "E71.4.41", {"start": v(11.47, -5.47) * mm, "end": v(14.82, -3.53) * mm});
            skLineSegment(sketch, "E71.4.42", {"start": v(22.52, -11.85) * mm, "end": v(22.52, -13) * mm});
            skLineSegment(sketch, "E71.4.43", {"start": v(11.32, -13.4) * mm, "end": v(14.14, -13.4) * mm, "construction": true});
            skLineSegment(sketch, "E71.4.44", {"start": v(17.26, -3.1) * mm, "end": v(18.67, -5.55) * mm, "construction": true});
            skLineSegment(sketch, "E71.4.45", {"start": v(21.52, -13.58) * mm, "end": v(22.52, -13) * mm});
            skLineSegment(sketch, "E71.4.46", {"start": v(9.94, -11.38) * mm, "end": v(9.4, -11.07) * mm});
            skLineSegment(sketch, "E71.4.47", {"start": v(12.73, -14.2) * mm, "end": v(12.73, -13.4) * mm, "construction": true});
            skLineSegment(sketch, "E71.4.48", {"start": v(23.33, -8.36) * mm, "end": v(23.33, -7.5) * mm});
            skLineSegment(sketch, "E71.4.49", {"start": v(9.4, -11.07) * mm, "end": v(10.47, -11.07) * mm, "construction": true});
            skLineSegment(sketch, "E71.4.50", {"start": v(14.82, -2.92) * mm, "end": v(14.56, -3.07) * mm, "construction": true});
            skLineSegment(sketch, "E71.4.51", {"start": v(14.82, -3.53) * mm, "end": v(14.82, -2.92) * mm});
            skLineSegment(sketch, "E71.4.52", {"start": v(14.82, -2.92) * mm, "end": v(14.29, -2.6) * mm});
            skLineSegment(sketch, "E71.4.53", {"start": v(14.14, -13.4) * mm, "end": v(12.73, -14.2) * mm});
            skLineSegment(sketch, "E71.4.54", {"start": v(18.67, -5.55) * mm, "end": v(18.67, -3.92) * mm});
            skLineSegment(sketch, "E71.4.55", {"start": v(18.67, -3.92) * mm, "end": v(17.26, -3.1) * mm});
            skLineSegment(sketch, "E71.4.56", {"start": v(9.94, -11.38) * mm, "end": v(9.94, -11.07) * mm, "construction": true});
            skLineSegment(sketch, "E71.4.57", {"start": v(18.15, -16.46) * mm, "end": v(18.15, -16.02) * mm, "construction": true});
            skLineSegment(sketch, "E71.4.58", {"start": v(17.4, -16.02) * mm, "end": v(18.9, -16.02) * mm, "construction": true});
            skLineSegment(sketch, "E71.4.59", {"start": v(23.33, -7.5) * mm, "end": v(22.58, -7.06) * mm});
            skLineSegment(sketch, "E71.4.60", {"start": v(14.29, -2.6) * mm, "end": v(14.82, -3.53) * mm, "construction": true});
            skLineSegment(sketch, "E71.4.61", {"start": v(10.47, -11.07) * mm, "end": v(9.94, -11.38) * mm});
            skLineSegment(sketch, "E71.4.62", {"start": v(18.9, -16.02) * mm, "end": v(18.15, -16.46) * mm});
            skLineSegment(sketch, "E71.4.63", {"start": v(18.15, -16.46) * mm, "end": v(17.4, -16.02) * mm});
            skLineSegment(sketch, "E71.4.64", {"start": v(22.58, -7.06) * mm, "end": v(23.33, -8.36) * mm, "construction": true});
            skLineSegment(sketch, "E71.4.65", {"start": v(12.73, -14.2) * mm, "end": v(11.32, -13.4) * mm});
            skLineSegment(sketch, "E71.4.66", {"start": v(18.67, -3.92) * mm, "end": v(17.96, -4.33) * mm, "construction": true});
            skLineSegment(sketch, "E71.4.67", {"start": v(23.33, -7.5) * mm, "end": v(22.95, -7.7) * mm, "construction": true});
            skLineSegment(sketch, "E71.5.0", {"start": v(7.21, -4.16) * mm, "end": v(7.21, 4.16) * mm});
            skLineSegment(sketch, "E71.5.1", {"start": v(14.14, 9.32) * mm, "end": v(14.14, 13.4) * mm});
            skLineSegment(sketch, "E71.5.2", {"start": v(8.21, 3.59) * mm, "end": v(22.52, 11.85) * mm});
            skLineSegment(sketch, "E71.5.3", {"start": v(20.65, 9.04) * mm, "end": v(17.51, 7.23) * mm});
            skLineSegment(sketch, "E71.5.4", {"start": v(9.4, 11.07) * mm, "end": v(9.4, 6.58) * mm});
            skPoint(sketch, "E71.5.5", {"position": v(17.96, 4.33) * mm});
            skLineSegment(sketch, "E71.5.6", {"start": v(18.15, 16.02) * mm, "end": v(18.15, 13.37) * mm, "construction": true});
            skLineSegment(sketch, "E71.5.7", {"start": v(17.26, 3.1) * mm, "end": v(12.32, 5.96) * mm});
            skLineSegment(sketch, "E71.5.8", {"start": v(0, 8.33) * mm, "end": v(7.21, 4.16) * mm});
            skLineSegment(sketch, "E71.5.9", {"start": v(15.14, 7.58) * mm, "end": v(18.67, 5.55) * mm});
            skLineSegment(sketch, "E71.5.10", {"start": v(0, 0) * mm, "end": v(8.21, 1.02) * mm});
            skLineSegment(sketch, "E71.5.11", {"start": v(2.08, 1.2) * mm, "end": v(2.08, -1.2) * mm});
            skLineSegment(sketch, "E71.5.12", {"start": v(0, 0) * mm, "end": v(8.21, 0) * mm, "construction": true});
            skLineSegment(sketch, "E71.5.13", {"start": v(8.21, 4.74) * mm, "end": v(8.21, -4.74) * mm});
            skLineSegment(sketch, "E71.5.14", {"start": v(20.65, 9.9) * mm, "end": v(23.33, 8.36) * mm});
            skPoint(sketch, "E71.5.15", {"position": v(12.73, 13.4) * mm});
            skLineSegment(sketch, "E71.5.16", {"start": v(17.51, 7.23) * mm, "end": v(16.01, 8.1) * mm});
            skLineSegment(sketch, "E71.5.17", {"start": v(8.21, 4.74) * mm, "end": v(0, 9.48) * mm});
            skLineSegment(sketch, "E71.5.21", {"start": v(2.08, 1.2) * mm, "end": v(0, 2.4) * mm});
            skLineSegment(sketch, "E71.5.22", {"start": v(7.21, 5.32) * mm, "end": v(21.52, 13.58) * mm});
            skLineSegment(sketch, "E71.5.23", {"start": v(18.15, 13.37) * mm, "end": v(15.01, 11.56) * mm});
            skLineSegment(sketch, "E71.5.24", {"start": v(15.01, 11.56) * mm, "end": v(15.01, 9.82) * mm});
            skLineSegment(sketch, "E71.5.25", {"start": v(10.7, 0.77) * mm, "end": v(13.75, 0.77) * mm});
            skLineSegment(sketch, "E71.5.26", {"start": v(11.32, 13.4) * mm, "end": v(11.32, 7.7) * mm});
            skLineSegment(sketch, "E71.5.27", {"start": v(17.4, 16.02) * mm, "end": v(17.4, 12.93) * mm});
            skLineSegment(sketch, "E71.5.28", {"start": v(22.95, 7.7) * mm, "end": v(20.65, 9.04) * mm, "construction": true});
            skLineSegment(sketch, "E71.5.29", {"start": v(22.58, 7.06) * mm, "end": v(19.9, 8.6) * mm});
            skLineSegment(sketch, "E71.5.30", {"start": v(12.04, 0) * mm, "end": v(8.21, 2.2) * mm});
            skLineSegment(sketch, "E71.5.31", {"start": v(6.02, 10.43) * mm, "end": v(6.02, 6) * mm});
            skLineSegment(sketch, "E71.5.32", {"start": v(14.29, 2.6) * mm, "end": v(10.4, 4.85) * mm});
            skLineSegment(sketch, "E71.5.33", {"start": v(0, 0) * mm, "end": v(8.21, -1.02) * mm});
            skLineSegment(sketch, "E71.5.34", {"start": v(6.02, 8.89) * mm, "end": v(7.54, 11.52) * mm});
            skLineSegment(sketch, "E71.5.35", {"start": v(20.65, 10.77) * mm, "end": v(20.65, 9.04) * mm});
            skLineSegment(sketch, "E71.5.36", {"start": v(18.9, 12.93) * mm, "end": v(18.9, 16.02) * mm});
            skLineSegment(sketch, "E71.5.37", {"start": v(11.47, 5.47) * mm, "end": v(14.82, 3.53) * mm});
            skLineSegment(sketch, "E71.5.38", {"start": v(7.54, 11.52) * mm, "end": v(7.1, 12.29) * mm});
            skLineSegment(sketch, "E71.5.39", {"start": v(19.65, 12.5) * mm, "end": v(18.15, 13.37) * mm});
            skLineSegment(sketch, "E71.5.40", {"start": v(13.75, 0.77) * mm, "end": v(14.2, 0) * mm});
            skLineSegment(sketch, "E71.5.41", {"start": v(10.47, 7.2) * mm, "end": v(10.47, 11.07) * mm});
            skLineSegment(sketch, "E71.5.42", {"start": v(21.52, 13.58) * mm, "end": v(22.52, 13) * mm});
            skLineSegment(sketch, "E71.5.43", {"start": v(17.26, 3.1) * mm, "end": v(18.67, 5.55) * mm, "construction": true});
            skLineSegment(sketch, "E71.5.44", {"start": v(11.32, 13.4) * mm, "end": v(14.14, 13.4) * mm, "construction": true});
            skLineSegment(sketch, "E71.5.45", {"start": v(22.52, 11.85) * mm, "end": v(22.52, 13) * mm});
            skLineSegment(sketch, "E71.5.46", {"start": v(14.82, 2.92) * mm, "end": v(14.29, 2.6) * mm});
            skLineSegment(sketch, "E71.5.47", {"start": v(18.67, 3.92) * mm, "end": v(17.96, 4.33) * mm, "construction": true});
            skLineSegment(sketch, "E71.5.48", {"start": v(18.9, 16.02) * mm, "end": v(18.15, 16.46) * mm});
            skLineSegment(sketch, "E71.5.49", {"start": v(14.29, 2.6) * mm, "end": v(14.82, 3.53) * mm, "construction": true});
            skLineSegment(sketch, "E71.5.50", {"start": v(9.94, 11.38) * mm, "end": v(9.94, 11.07) * mm, "construction": true});
            skLineSegment(sketch, "E71.5.51", {"start": v(10.47, 11.07) * mm, "end": v(9.94, 11.38) * mm});
            skLineSegment(sketch, "E71.5.52", {"start": v(9.94, 11.38) * mm, "end": v(9.4, 11.07) * mm});
            skLineSegment(sketch, "E71.5.53", {"start": v(18.67, 5.55) * mm, "end": v(18.67, 3.92) * mm});
            skLineSegment(sketch, "E71.5.54", {"start": v(14.14, 13.4) * mm, "end": v(12.73, 14.2) * mm});
            skLineSegment(sketch, "E71.5.55", {"start": v(12.73, 14.2) * mm, "end": v(11.32, 13.4) * mm});
            skLineSegment(sketch, "E71.5.56", {"start": v(14.82, 2.92) * mm, "end": v(14.56, 3.07) * mm, "construction": true});
            skLineSegment(sketch, "E71.5.57", {"start": v(23.33, 7.5) * mm, "end": v(22.95, 7.7) * mm, "construction": true});
            skLineSegment(sketch, "E71.5.58", {"start": v(22.58, 7.06) * mm, "end": v(23.33, 8.36) * mm, "construction": true});
            skLineSegment(sketch, "E71.5.59", {"start": v(18.15, 16.46) * mm, "end": v(17.4, 16.02) * mm});
            skLineSegment(sketch, "E71.5.60", {"start": v(9.4, 11.07) * mm, "end": v(10.47, 11.07) * mm, "construction": true});
            skLineSegment(sketch, "E71.5.61", {"start": v(14.82, 3.53) * mm, "end": v(14.82, 2.92) * mm});
            skLineSegment(sketch, "E71.5.62", {"start": v(23.33, 8.36) * mm, "end": v(23.33, 7.5) * mm});
            skLineSegment(sketch, "E71.5.63", {"start": v(23.33, 7.5) * mm, "end": v(22.58, 7.06) * mm});
            skLineSegment(sketch, "E71.5.64", {"start": v(17.4, 16.02) * mm, "end": v(18.9, 16.02) * mm, "construction": true});
            skLineSegment(sketch, "E71.5.65", {"start": v(18.67, 3.92) * mm, "end": v(17.26, 3.1) * mm});
            skLineSegment(sketch, "E71.5.66", {"start": v(12.73, 14.2) * mm, "end": v(12.73, 13.4) * mm, "construction": true});
            skLineSegment(sketch, "E71.5.67", {"start": v(18.15, 16.46) * mm, "end": v(18.15, 16.02) * mm, "construction": true});
            skPoint(sketch, "E71.center", {"position": v(0, 0) * mm});
            skSolve(sketch);
        }
        {
            var Q0;
            {var subQ0=sQuery(id+"F0.wireOp",EDGE,"E26");Q0=makeQuery(id+"F0.imprint","IMPRINT",FACE,{"disambiguationData":[TD([[makeQuery(id+"F0.imprint","IMPRINT",EDGE,{"derivedFrom":subQ0}),1.0]])]});}
            var Q1;
            {var subQ0=sQuery(id+"F0.wireOp",EDGE,"E20");Q1=makeQuery(id+"F0.imprint","IMPRINT",FACE,{"disambiguationData":[TD([[makeQuery(id+"F0.imprint","IMPRINT",EDGE,{"derivedFrom":subQ0}),1.0]])]});}
            var Q2;
            {var subQ0=sQuery(id+"F0.wireOp",EDGE,"E13");Q2=makeQuery(id+"F0.imprint","IMPRINT",FACE,{"disambiguationData":[TD([[makeQuery(id+"F0.imprint","IMPRINT",EDGE,{"derivedFrom":subQ0}),1.0]])]});}
            var Q3;
            {var subQ1=sQuery(id+"F0.wireOp",EDGE,"E34");Q3=makeQuery(id+"F0.imprint","IMPRINT",FACE,{"disambiguationData":[TD([[makeQuery(id+"F0.imprint","IMPRINT",EDGE,{"derivedFrom":subQ1}),1.0]])]});}
            var Q4;
            Q4=makeQuery(id+"F0.imprint","IMPRINT",FACE,{"disambiguationData":[TD([[makeQuery(id+"F0.imprint","IMPRINT",EDGE,{"derivedFrom":sQuery(id+"F0.wireOp",EDGE,"E39.MirrorCS")}),-1.0]])]});
            var Q5;
            Q5=makeQuery(id+"F0.imprint","IMPRINT",FACE,{"disambiguationData":[TD([[makeQuery(id+"F0.imprint","IMPRINT",EDGE,{"derivedFrom":sQuery(id+"F0.wireOp",EDGE,"E41.MirrorCS")}),-1.0]])]});
            var Q6;
            Q6=makeQuery(id+"F0.imprint","IMPRINT",FACE,{"disambiguationData":[TD([[makeQuery(id+"F0.imprint","IMPRINT",EDGE,{"derivedFrom":sQuery(id+"F0.wireOp",EDGE,"E43.MirrorCS")}),-1.0]])]});
            var Q7;
            Q7=makeQuery(id+"F0.imprint","IMPRINT",FACE,{"disambiguationData":[TD([[makeQuery(id+"F0.imprint","IMPRINT",EDGE,{"derivedFrom":sQuery(id+"F0.wireOp",EDGE,"E50.MirrorCS")}),-1.0]])]});
            var Q8;
            {var subQ2=sQuery(id+"F0.wireOp",EDGE,"E71.1.1");Q8=makeQuery(id+"F0.imprint","IMPRINT",FACE,{"disambiguationData":[TD([[makeQuery(id+"F0.imprint","IMPRINT",EDGE,{"derivedFrom":subQ2}),1.0]])]});}
            var Q9;
            {var subQ1=sQuery(id+"F0.wireOp",EDGE,"E71.1.32");Q9=makeQuery(id+"F0.imprint","IMPRINT",FACE,{"disambiguationData":[TD([[makeQuery(id+"F0.imprint","IMPRINT",EDGE,{"derivedFrom":subQ1}),-1.0]])]});}
            var Q10;
            {var subQ1=sQuery(id+"F0.wireOp",EDGE,"E71.1.7");Q10=makeQuery(id+"F0.imprint","IMPRINT",FACE,{"disambiguationData":[TD([[makeQuery(id+"F0.imprint","IMPRINT",EDGE,{"derivedFrom":subQ1}),-1.0]])]});}
            var Q11;
            {var subQ3=sQuery(id+"F0.wireOp",EDGE,"E71.1.14");Q11=makeQuery(id+"F0.imprint","IMPRINT",FACE,{"disambiguationData":[TD([[makeQuery(id+"F0.imprint","IMPRINT",EDGE,{"derivedFrom":subQ3}),-1.0]])]});}
            var Q12;
            {var subQ2=sQuery(id+"F0.wireOp",EDGE,"E71.1.4");Q12=makeQuery(id+"F0.imprint","IMPRINT",FACE,{"disambiguationData":[TD([[makeQuery(id+"F0.imprint","IMPRINT",EDGE,{"derivedFrom":subQ2}),1.0]])]});}
            var Q13;
            {var subQ4=sQuery(id+"F0.wireOp",EDGE,"E71.1.27");Q13=makeQuery(id+"F0.imprint","IMPRINT",FACE,{"disambiguationData":[TD([[makeQuery(id+"F0.imprint","IMPRINT",EDGE,{"derivedFrom":subQ4}),1.0]])]});}
            var Q14;
            {var subQ4=sQuery(id+"F0.wireOp",EDGE,"E71.1.34");Q14=makeQuery(id+"F0.imprint","IMPRINT",FACE,{"disambiguationData":[TD([[makeQuery(id+"F0.imprint","IMPRINT",EDGE,{"derivedFrom":subQ4}),1.0]])]});}
            var Q15;
            {var subQ2=sQuery(id+"F0.wireOp",EDGE,"E71.2.1");Q15=makeQuery(id+"F0.imprint","IMPRINT",FACE,{"disambiguationData":[TD([[makeQuery(id+"F0.imprint","IMPRINT",EDGE,{"derivedFrom":subQ2}),1.0]])]});}
            var Q16;
            {var subQ1=sQuery(id+"F0.wireOp",EDGE,"E71.2.32");Q16=makeQuery(id+"F0.imprint","IMPRINT",FACE,{"disambiguationData":[TD([[makeQuery(id+"F0.imprint","IMPRINT",EDGE,{"derivedFrom":subQ1}),-1.0]])]});}
            var Q17;
            {var subQ1=sQuery(id+"F0.wireOp",EDGE,"E71.2.7");Q17=makeQuery(id+"F0.imprint","IMPRINT",FACE,{"disambiguationData":[TD([[makeQuery(id+"F0.imprint","IMPRINT",EDGE,{"derivedFrom":subQ1}),-1.0]])]});}
            var Q18;
            {var subQ3=sQuery(id+"F0.wireOp",EDGE,"E71.2.14");Q18=makeQuery(id+"F0.imprint","IMPRINT",FACE,{"disambiguationData":[TD([[makeQuery(id+"F0.imprint","IMPRINT",EDGE,{"derivedFrom":subQ3}),-1.0]])]});}
            var Q19;
            {var subQ2=sQuery(id+"F0.wireOp",EDGE,"E71.2.4");Q19=makeQuery(id+"F0.imprint","IMPRINT",FACE,{"disambiguationData":[TD([[makeQuery(id+"F0.imprint","IMPRINT",EDGE,{"derivedFrom":subQ2}),1.0]])]});}
            var Q20;
            {var subQ4=sQuery(id+"F0.wireOp",EDGE,"E71.2.27");Q20=makeQuery(id+"F0.imprint","IMPRINT",FACE,{"disambiguationData":[TD([[makeQuery(id+"F0.imprint","IMPRINT",EDGE,{"derivedFrom":subQ4}),1.0]])]});}
            var Q21;
            {var subQ4=sQuery(id+"F0.wireOp",EDGE,"E71.2.34");Q21=makeQuery(id+"F0.imprint","IMPRINT",FACE,{"disambiguationData":[TD([[makeQuery(id+"F0.imprint","IMPRINT",EDGE,{"derivedFrom":subQ4}),1.0]])]});}
            var Q22;
            {var subQ2=sQuery(id+"F0.wireOp",EDGE,"E71.3.1");Q22=makeQuery(id+"F0.imprint","IMPRINT",FACE,{"disambiguationData":[TD([[makeQuery(id+"F0.imprint","IMPRINT",EDGE,{"derivedFrom":subQ2}),1.0]])]});}
            var Q23;
            {var subQ1=sQuery(id+"F0.wireOp",EDGE,"E71.3.32");Q23=makeQuery(id+"F0.imprint","IMPRINT",FACE,{"disambiguationData":[TD([[makeQuery(id+"F0.imprint","IMPRINT",EDGE,{"derivedFrom":subQ1}),-1.0]])]});}
            var Q24;
            {var subQ1=sQuery(id+"F0.wireOp",EDGE,"E71.3.7");Q24=makeQuery(id+"F0.imprint","IMPRINT",FACE,{"disambiguationData":[TD([[makeQuery(id+"F0.imprint","IMPRINT",EDGE,{"derivedFrom":subQ1}),-1.0]])]});}
            var Q25;
            {var subQ3=sQuery(id+"F0.wireOp",EDGE,"E71.3.14");Q25=makeQuery(id+"F0.imprint","IMPRINT",FACE,{"disambiguationData":[TD([[makeQuery(id+"F0.imprint","IMPRINT",EDGE,{"derivedFrom":subQ3}),-1.0]])]});}
            var Q26;
            {var subQ2=sQuery(id+"F0.wireOp",EDGE,"E71.3.4");Q26=makeQuery(id+"F0.imprint","IMPRINT",FACE,{"disambiguationData":[TD([[makeQuery(id+"F0.imprint","IMPRINT",EDGE,{"derivedFrom":subQ2}),1.0]])]});}
            var Q27;
            {var subQ4=sQuery(id+"F0.wireOp",EDGE,"E71.3.27");Q27=makeQuery(id+"F0.imprint","IMPRINT",FACE,{"disambiguationData":[TD([[makeQuery(id+"F0.imprint","IMPRINT",EDGE,{"derivedFrom":subQ4}),1.0]])]});}
            var Q28;
            {var subQ4=sQuery(id+"F0.wireOp",EDGE,"E71.3.34");Q28=makeQuery(id+"F0.imprint","IMPRINT",FACE,{"disambiguationData":[TD([[makeQuery(id+"F0.imprint","IMPRINT",EDGE,{"derivedFrom":subQ4}),1.0]])]});}
            var Q29;
            {var subQ2=sQuery(id+"F0.wireOp",EDGE,"E71.4.1");Q29=makeQuery(id+"F0.imprint","IMPRINT",FACE,{"disambiguationData":[TD([[makeQuery(id+"F0.imprint","IMPRINT",EDGE,{"derivedFrom":subQ2}),1.0]])]});}
            var Q30;
            {var subQ1=sQuery(id+"F0.wireOp",EDGE,"E71.4.32");Q30=makeQuery(id+"F0.imprint","IMPRINT",FACE,{"disambiguationData":[TD([[makeQuery(id+"F0.imprint","IMPRINT",EDGE,{"derivedFrom":subQ1}),-1.0]])]});}
            var Q31;
            {var subQ1=sQuery(id+"F0.wireOp",EDGE,"E71.4.7");Q31=makeQuery(id+"F0.imprint","IMPRINT",FACE,{"disambiguationData":[TD([[makeQuery(id+"F0.imprint","IMPRINT",EDGE,{"derivedFrom":subQ1}),-1.0]])]});}
            var Q32;
            {var subQ3=sQuery(id+"F0.wireOp",EDGE,"E71.4.14");Q32=makeQuery(id+"F0.imprint","IMPRINT",FACE,{"disambiguationData":[TD([[makeQuery(id+"F0.imprint","IMPRINT",EDGE,{"derivedFrom":subQ3}),-1.0]])]});}
            var Q33;
            {var subQ2=sQuery(id+"F0.wireOp",EDGE,"E71.4.4");Q33=makeQuery(id+"F0.imprint","IMPRINT",FACE,{"disambiguationData":[TD([[makeQuery(id+"F0.imprint","IMPRINT",EDGE,{"derivedFrom":subQ2}),1.0]])]});}
            var Q34;
            {var subQ4=sQuery(id+"F0.wireOp",EDGE,"E71.4.27");Q34=makeQuery(id+"F0.imprint","IMPRINT",FACE,{"disambiguationData":[TD([[makeQuery(id+"F0.imprint","IMPRINT",EDGE,{"derivedFrom":subQ4}),1.0]])]});}
            var Q35;
            {var subQ3=sQuery(id+"F0.wireOp",EDGE,"E71.4.34");Q35=makeQuery(id+"F0.imprint","IMPRINT",FACE,{"disambiguationData":[TD([[makeQuery(id+"F0.imprint","IMPRINT",EDGE,{"derivedFrom":subQ3}),1.0]])]});}
            var Q36;
            {var subQ2=sQuery(id+"F0.wireOp",EDGE,"E71.5.1");Q36=makeQuery(id+"F0.imprint","IMPRINT",FACE,{"disambiguationData":[TD([[makeQuery(id+"F0.imprint","IMPRINT",EDGE,{"derivedFrom":subQ2}),1.0]])]});}
            var Q37;
            {var subQ1=sQuery(id+"F0.wireOp",EDGE,"E71.5.32");Q37=makeQuery(id+"F0.imprint","IMPRINT",FACE,{"disambiguationData":[TD([[makeQuery(id+"F0.imprint","IMPRINT",EDGE,{"derivedFrom":subQ1}),-1.0]])]});}
            var Q38;
            {var subQ1=sQuery(id+"F0.wireOp",EDGE,"E71.5.7");Q38=makeQuery(id+"F0.imprint","IMPRINT",FACE,{"disambiguationData":[TD([[makeQuery(id+"F0.imprint","IMPRINT",EDGE,{"derivedFrom":subQ1}),-1.0]])]});}
            var Q39;
            {var subQ3=sQuery(id+"F0.wireOp",EDGE,"E71.5.14");Q39=makeQuery(id+"F0.imprint","IMPRINT",FACE,{"disambiguationData":[TD([[makeQuery(id+"F0.imprint","IMPRINT",EDGE,{"derivedFrom":subQ3}),-1.0]])]});}
            var Q40;
            {var subQ2=sQuery(id+"F0.wireOp",EDGE,"E71.5.4");Q40=makeQuery(id+"F0.imprint","IMPRINT",FACE,{"disambiguationData":[TD([[makeQuery(id+"F0.imprint","IMPRINT",EDGE,{"derivedFrom":subQ2}),1.0]])]});}
            var Q41;
            {var subQ4=sQuery(id+"F0.wireOp",EDGE,"E71.5.27");Q41=makeQuery(id+"F0.imprint","IMPRINT",FACE,{"disambiguationData":[TD([[makeQuery(id+"F0.imprint","IMPRINT",EDGE,{"derivedFrom":subQ4}),1.0]])]});}
            var Q42;
            {var subQ7=sQuery(id+"F0.wireOp",EDGE,"E12");Q42=makeQuery(id+"F0.imprint","IMPRINT",FACE,{"disambiguationData":[TD([[makeQuery(id+"F0.imprint","IMPRINT",EDGE,{"derivedFrom":subQ7}),1.0]])]});}
            var Q43;
            {var subQ4=sQuery(id+"F0.wireOp",EDGE,"E54.MirrorCS");Q43=makeQuery(id+"F0.imprint","IMPRINT",FACE,{"disambiguationData":[TD([[makeQuery(id+"F0.imprint","IMPRINT",EDGE,{"derivedFrom":subQ4}),-1.0]])]});}
            var Q44;
            {var subQ0=sQuery(id+"F0.wireOp",EDGE,"E71.1.16");Q44=makeQuery(id+"F0.imprint","IMPRINT",FACE,{"disambiguationData":[TD([[makeQuery(id+"F0.imprint","IMPRINT",EDGE,{"derivedFrom":subQ0}),-1.0]])]});}
            var Q45;
            {var subQ0=sQuery(id+"F0.wireOp",EDGE,"E71.1.24");Q45=makeQuery(id+"F0.imprint","IMPRINT",FACE,{"disambiguationData":[TD([[makeQuery(id+"F0.imprint","IMPRINT",EDGE,{"derivedFrom":subQ0}),1.0]])]});}
            var Q46;
            {var subQ0=sQuery(id+"F0.wireOp",EDGE,"E71.2.16");Q46=makeQuery(id+"F0.imprint","IMPRINT",FACE,{"disambiguationData":[TD([[makeQuery(id+"F0.imprint","IMPRINT",EDGE,{"derivedFrom":subQ0}),-1.0]])]});}
            var Q47;
            {var subQ0=sQuery(id+"F0.wireOp",EDGE,"E71.2.24");Q47=makeQuery(id+"F0.imprint","IMPRINT",FACE,{"disambiguationData":[TD([[makeQuery(id+"F0.imprint","IMPRINT",EDGE,{"derivedFrom":subQ0}),1.0]])]});}
            var Q48;
            {var subQ0=sQuery(id+"F0.wireOp",EDGE,"E71.3.16");Q48=makeQuery(id+"F0.imprint","IMPRINT",FACE,{"disambiguationData":[TD([[makeQuery(id+"F0.imprint","IMPRINT",EDGE,{"derivedFrom":subQ0}),-1.0]])]});}
            var Q49;
            {var subQ0=sQuery(id+"F0.wireOp",EDGE,"E71.3.24");Q49=makeQuery(id+"F0.imprint","IMPRINT",FACE,{"disambiguationData":[TD([[makeQuery(id+"F0.imprint","IMPRINT",EDGE,{"derivedFrom":subQ0}),1.0]])]});}
            var Q50;
            {var subQ0=sQuery(id+"F0.wireOp",EDGE,"E71.4.16");Q50=makeQuery(id+"F0.imprint","IMPRINT",FACE,{"disambiguationData":[TD([[makeQuery(id+"F0.imprint","IMPRINT",EDGE,{"derivedFrom":subQ0}),-1.0]])]});}
            var Q51;
            {var subQ0=sQuery(id+"F0.wireOp",EDGE,"E71.4.24");Q51=makeQuery(id+"F0.imprint","IMPRINT",FACE,{"disambiguationData":[TD([[makeQuery(id+"F0.imprint","IMPRINT",EDGE,{"derivedFrom":subQ0}),1.0]])]});}
            var Q52;
            {var subQ0=sQuery(id+"F0.wireOp",EDGE,"E71.5.16");Q52=makeQuery(id+"F0.imprint","IMPRINT",FACE,{"disambiguationData":[TD([[makeQuery(id+"F0.imprint","IMPRINT",EDGE,{"derivedFrom":subQ0}),-1.0]])]});}
            var Q53;
            {var subQ0=sQuery(id+"F0.wireOp",EDGE,"E71.5.24");Q53=makeQuery(id+"F0.imprint","IMPRINT",FACE,{"disambiguationData":[TD([[makeQuery(id+"F0.imprint","IMPRINT",EDGE,{"derivedFrom":subQ0}),1.0]])]});}
            var Q54;
            {var subQ3=sQuery(id+"F0.wireOp",EDGE,"E71.1.30");var subQ6=sQuery(id+"F0.wireOp",EDGE,"E33");var subQ9=makeQuery(id+"F0.imprint","INTERSECT",VERTEX,{"derivedFrom":[subQ6,subQ3]});Q54=makeQuery(id+"F0.imprint","IMPRINT",FACE,{"disambiguationData":[TD([[makeQuery(id+"F0.imprint","IMPRINT",EDGE,{"disambiguationData":[TD([[subQ9,-1.0]])],"derivedFrom":subQ6}),-1.0]])]});}
            var Q55;
            {var subQ5=sQuery(id+"F0.wireOp",EDGE,"E66.MirrorCS");var subQ6=makeQuery(id+"F0.imprint","INTERSECT",VERTEX,{"derivedFrom":[sQuery(id+"F0.wireOp",EDGE,"E55.MirrorCS"),subQ5]});Q55=makeQuery(id+"F0.imprint","IMPRINT",FACE,{"disambiguationData":[TD([[makeQuery(id+"F0.imprint","IMPRINT",EDGE,{"disambiguationData":[TD([[subQ6,1.0]])],"derivedFrom":subQ5}),1.0]])]});}
            var Q56;
            {var subQ2=sQuery(id+"F0.wireOp",EDGE,"E71.2.30");var subQ5=sQuery(id+"F0.wireOp",EDGE,"E71.1.31");var subQ9=makeQuery(id+"F0.imprint","INTERSECT",VERTEX,{"derivedFrom":[subQ5,subQ2]});Q56=makeQuery(id+"F0.imprint","IMPRINT",FACE,{"disambiguationData":[TD([[makeQuery(id+"F0.imprint","IMPRINT",EDGE,{"disambiguationData":[TD([[subQ9,-1.0]])],"derivedFrom":subQ5}),-1.0]])]});}
            var Q57;
            {var subQ2=sQuery(id+"F0.wireOp",EDGE,"E71.3.30");var subQ5=sQuery(id+"F0.wireOp",EDGE,"E71.2.31");var subQ9=makeQuery(id+"F0.imprint","INTERSECT",VERTEX,{"derivedFrom":[subQ5,subQ2]});Q57=makeQuery(id+"F0.imprint","IMPRINT",FACE,{"disambiguationData":[TD([[makeQuery(id+"F0.imprint","IMPRINT",EDGE,{"disambiguationData":[TD([[subQ9,-1.0]])],"derivedFrom":subQ5}),-1.0]])]});}
            var Q58;
            {var subQ2=sQuery(id+"F0.wireOp",EDGE,"E71.4.30");var subQ5=sQuery(id+"F0.wireOp",EDGE,"E71.3.31");var subQ9=makeQuery(id+"F0.imprint","INTERSECT",VERTEX,{"derivedFrom":[subQ5,subQ2]});Q58=makeQuery(id+"F0.imprint","IMPRINT",FACE,{"disambiguationData":[TD([[makeQuery(id+"F0.imprint","IMPRINT",EDGE,{"disambiguationData":[TD([[subQ9,-1.0]])],"derivedFrom":subQ5}),-1.0]])]});}
            var Q59;
            {var subQ3=sQuery(id+"F0.wireOp",EDGE,"E71.5.30");var subQ5=sQuery(id+"F0.wireOp",EDGE,"E71.4.31");var subQ8=makeQuery(id+"F0.imprint","INTERSECT",VERTEX,{"derivedFrom":[subQ5,subQ3]});Q59=makeQuery(id+"F0.imprint","IMPRINT",FACE,{"disambiguationData":[TD([[makeQuery(id+"F0.imprint","IMPRINT",EDGE,{"disambiguationData":[TD([[subQ8,-1.0]])],"derivedFrom":subQ5}),-1.0]])]});}
            var Q60;
            {var subQ11=sQuery(id+"F0.wireOp",EDGE,"E71.5.8");var subQ12=sQuery(id+"F0.wireOp",EDGE,"E71.1.0");var subQ13=makeQuery(id+"F0.imprint","INTERSECT",VERTEX,{"derivedFrom":[subQ12,subQ11]});Q60=makeQuery(id+"F0.imprint","IMPRINT",FACE,{"disambiguationData":[TD([[makeQuery(id+"F0.imprint","IMPRINT",EDGE,{"disambiguationData":[TD([[subQ13,-1.0]])],"derivedFrom":subQ12}),-1.0]])]});}
            var Q61;
            {var subQ5=sQuery(id+"F0.wireOp",EDGE,"E71.1.0");var subQ9=sQuery(id+"F0.wireOp",EDGE,"E71.2.0");var subQ10=makeQuery(id+"F0.imprint","INTERSECT",VERTEX,{"derivedFrom":[subQ5,subQ9]});Q61=makeQuery(id+"F0.imprint","IMPRINT",FACE,{"disambiguationData":[TD([[makeQuery(id+"F0.imprint","IMPRINT",EDGE,{"disambiguationData":[TD([[subQ10,1.0]])],"derivedFrom":subQ5}),-1.0]])]});}
            var Q62;
            {var subQ5=sQuery(id+"F0.wireOp",EDGE,"E71.2.0");var subQ9=sQuery(id+"F0.wireOp",EDGE,"E71.3.0");var subQ10=makeQuery(id+"F0.imprint","INTERSECT",VERTEX,{"derivedFrom":[subQ5,subQ9]});Q62=makeQuery(id+"F0.imprint","IMPRINT",FACE,{"disambiguationData":[TD([[makeQuery(id+"F0.imprint","IMPRINT",EDGE,{"disambiguationData":[TD([[subQ10,1.0]])],"derivedFrom":subQ5}),-1.0]])]});}
            var Q63;
            {var subQ5=sQuery(id+"F0.wireOp",EDGE,"E71.3.0");var subQ9=sQuery(id+"F0.wireOp",EDGE,"E71.4.0");var subQ10=makeQuery(id+"F0.imprint","INTERSECT",VERTEX,{"derivedFrom":[subQ5,subQ9]});Q63=makeQuery(id+"F0.imprint","IMPRINT",FACE,{"disambiguationData":[TD([[makeQuery(id+"F0.imprint","IMPRINT",EDGE,{"disambiguationData":[TD([[subQ10,1.0]])],"derivedFrom":subQ5}),-1.0]])]});}
            var Q64;
            {var subQ5=sQuery(id+"F0.wireOp",EDGE,"E71.4.0");var subQ12=sQuery(id+"F0.wireOp",EDGE,"E71.5.0");var subQ13=makeQuery(id+"F0.imprint","INTERSECT",VERTEX,{"derivedFrom":[subQ5,subQ12]});Q64=makeQuery(id+"F0.imprint","IMPRINT",FACE,{"disambiguationData":[TD([[makeQuery(id+"F0.imprint","IMPRINT",EDGE,{"disambiguationData":[TD([[subQ13,1.0]])],"derivedFrom":subQ5}),-1.0]])]});}
            var Q65;
            {var subQ9=sQuery(id+"F0.wireOp",EDGE,"E71.5.0");var subQ11=sQuery(id+"F0.wireOp",EDGE,"E71.5.8");var subQ13=makeQuery(id+"F0.imprint","INTERSECT",VERTEX,{"derivedFrom":[subQ9,subQ11]});Q65=makeQuery(id+"F0.imprint","IMPRINT",FACE,{"disambiguationData":[TD([[makeQuery(id+"F0.imprint","IMPRINT",EDGE,{"disambiguationData":[TD([[subQ13,1.0]])],"derivedFrom":subQ9}),-1.0]])]});}
            var Q66;
            {var subQ7=sQuery(id+"F0.wireOp",EDGE,"E9");Q66=makeQuery(id+"F0.imprint","IMPRINT",FACE,{"disambiguationData":[TD([[makeQuery(id+"F0.imprint","IMPRINT",EDGE,{"derivedFrom":subQ7}),-1.0]])]});}
            var Q67;
            {var subQ20=sQuery(id+"F0.wireOp",EDGE,"E71.1.42");Q67=makeQuery(id+"F0.imprint","IMPRINT",FACE,{"disambiguationData":[TD([[makeQuery(id+"F0.imprint","IMPRINT",EDGE,{"derivedFrom":subQ20}),-1.0]])]});}
            var Q68;
            {var subQ20=sQuery(id+"F0.wireOp",EDGE,"E71.2.42");Q68=makeQuery(id+"F0.imprint","IMPRINT",FACE,{"disambiguationData":[TD([[makeQuery(id+"F0.imprint","IMPRINT",EDGE,{"derivedFrom":subQ20}),-1.0]])]});}
            var Q69;
            {var subQ20=sQuery(id+"F0.wireOp",EDGE,"E71.3.42");Q69=makeQuery(id+"F0.imprint","IMPRINT",FACE,{"disambiguationData":[TD([[makeQuery(id+"F0.imprint","IMPRINT",EDGE,{"derivedFrom":subQ20}),-1.0]])]});}
            var Q70;
            {var subQ20=sQuery(id+"F0.wireOp",EDGE,"E71.4.42");Q70=makeQuery(id+"F0.imprint","IMPRINT",FACE,{"disambiguationData":[TD([[makeQuery(id+"F0.imprint","IMPRINT",EDGE,{"derivedFrom":subQ20}),-1.0]])]});}
            var Q71;
            {var subQ9=sQuery(id+"F0.wireOp",EDGE,"E71.5.42");Q71=makeQuery(id+"F0.imprint","IMPRINT",FACE,{"disambiguationData":[TD([[makeQuery(id+"F0.imprint","IMPRINT",EDGE,{"derivedFrom":subQ9}),-1.0]])]});}
            var Q72;
            {var subQ0=sQuery(id+"F0.wireOp",EDGE,"E5");var subQ1=sQuery(id+"F0.wireOp",EDGE,"E71.1.0");var subQ2=makeQuery(id+"F0.imprint","INTERSECT",VERTEX,{"derivedFrom":[subQ1,subQ0]});Q72=makeQuery(id+"F0.imprint","IMPRINT",FACE,{"disambiguationData":[TD([[makeQuery(id+"F0.imprint","IMPRINT",EDGE,{"disambiguationData":[TD([[subQ2,-1.0]])],"derivedFrom":subQ1}),-1.0]])]});}
            var Q73;
            {var subQ0=sQuery(id+"F0.wireOp",EDGE,"E71.2.33");var subQ1=sQuery(id+"F0.wireOp",EDGE,"E71.2.0");var subQ2=makeQuery(id+"F0.imprint","INTERSECT",VERTEX,{"derivedFrom":[subQ1,subQ0]});Q73=makeQuery(id+"F0.imprint","IMPRINT",FACE,{"disambiguationData":[TD([[makeQuery(id+"F0.imprint","IMPRINT",EDGE,{"disambiguationData":[TD([[subQ2,-1.0]])],"derivedFrom":subQ1}),-1.0]])]});}
            var Q74;
            {var subQ0=sQuery(id+"F0.wireOp",EDGE,"E71.3.33");var subQ1=sQuery(id+"F0.wireOp",EDGE,"E71.3.0");var subQ2=makeQuery(id+"F0.imprint","INTERSECT",VERTEX,{"derivedFrom":[subQ1,subQ0]});Q74=makeQuery(id+"F0.imprint","IMPRINT",FACE,{"disambiguationData":[TD([[makeQuery(id+"F0.imprint","IMPRINT",EDGE,{"disambiguationData":[TD([[subQ2,-1.0]])],"derivedFrom":subQ1}),-1.0]])]});}
            var Q75;
            {var subQ0=sQuery(id+"F0.wireOp",EDGE,"E71.4.33");var subQ1=sQuery(id+"F0.wireOp",EDGE,"E71.4.0");var subQ2=makeQuery(id+"F0.imprint","INTERSECT",VERTEX,{"derivedFrom":[subQ1,subQ0]});Q75=makeQuery(id+"F0.imprint","IMPRINT",FACE,{"disambiguationData":[TD([[makeQuery(id+"F0.imprint","IMPRINT",EDGE,{"disambiguationData":[TD([[subQ2,-1.0]])],"derivedFrom":subQ1}),-1.0]])]});}
            var Q76;
            {var subQ0=sQuery(id+"F0.wireOp",EDGE,"E71.5.33");var subQ1=sQuery(id+"F0.wireOp",EDGE,"E71.5.0");var subQ2=makeQuery(id+"F0.imprint","INTERSECT",VERTEX,{"derivedFrom":[subQ1,subQ0]});Q76=makeQuery(id+"F0.imprint","IMPRINT",FACE,{"disambiguationData":[TD([[makeQuery(id+"F0.imprint","IMPRINT",EDGE,{"disambiguationData":[TD([[subQ2,-1.0]])],"derivedFrom":subQ1}),-1.0]])]});}
            var Q77;
            {var subQ0=sQuery(id+"F0.wireOp",EDGE,"E68.MirrorCS");var subQ1=sQuery(id+"F0.wireOp",EDGE,"E71.5.8");var subQ2=makeQuery(id+"F0.imprint","INTERSECT",VERTEX,{"derivedFrom":[subQ1,subQ0]});Q77=makeQuery(id+"F0.imprint","IMPRINT",FACE,{"disambiguationData":[TD([[makeQuery(id+"F0.imprint","IMPRINT",EDGE,{"disambiguationData":[TD([[subQ2,-1.0]])],"derivedFrom":subQ1}),1.0]])]});}
            var Q78;
            {var subQ0=sQuery(id+"F0.wireOp",EDGE,"E68.MirrorCS");var subQ1=sQuery(id+"F0.wireOp",EDGE,"E71.5.8");var subQ2=makeQuery(id+"F0.imprint","INTERSECT",VERTEX,{"derivedFrom":[subQ1,subQ0]});Q78=makeQuery(id+"F0.imprint","IMPRINT",FACE,{"disambiguationData":[TD([[makeQuery(id+"F0.imprint","IMPRINT",EDGE,{"disambiguationData":[TD([[subQ2,-1.0]])],"derivedFrom":subQ1}),-1.0]])]});}
            var Q79;
            {var subQ0=sQuery(id+"F0.wireOp",EDGE,"E71.2.33");var subQ1=sQuery(id+"F0.wireOp",EDGE,"E71.2.0");var subQ2=makeQuery(id+"F0.imprint","INTERSECT",VERTEX,{"derivedFrom":[subQ1,subQ0]});Q79=makeQuery(id+"F0.imprint","IMPRINT",FACE,{"disambiguationData":[TD([[makeQuery(id+"F0.imprint","IMPRINT",EDGE,{"disambiguationData":[TD([[subQ2,-1.0]])],"derivedFrom":subQ1}),1.0]])]});}
            var Q80;
            {var subQ3=sQuery(id+"F0.wireOp",EDGE,"E71.3.11");var subQ5=sQuery(id+"F0.wireOp",EDGE,"E71.4.11");var subQ6=makeQuery(id+"F0.imprint","INTERSECT",VERTEX,{"derivedFrom":[subQ3,subQ5]});Q80=makeQuery(id+"F0.imprint","IMPRINT",FACE,{"disambiguationData":[TD([[makeQuery(id+"F0.imprint","IMPRINT",EDGE,{"disambiguationData":[TD([[subQ6,-1.0]])],"derivedFrom":subQ3}),-1.0]])]});}
            var Q81;
            {var subQ0=sQuery(id+"F0.wireOp",EDGE,"E5");var subQ1=sQuery(id+"F0.wireOp",EDGE,"E71.1.0");var subQ2=makeQuery(id+"F0.imprint","INTERSECT",VERTEX,{"derivedFrom":[subQ1,subQ0]});Q81=makeQuery(id+"F0.imprint","IMPRINT",FACE,{"disambiguationData":[TD([[makeQuery(id+"F0.imprint","IMPRINT",EDGE,{"disambiguationData":[TD([[subQ2,-1.0]])],"derivedFrom":subQ1}),1.0]])]});}
            var Q82;
            {var subQ0=sQuery(id+"F0.wireOp",EDGE,"E71.5.33");var subQ1=sQuery(id+"F0.wireOp",EDGE,"E71.5.0");var subQ2=makeQuery(id+"F0.imprint","INTERSECT",VERTEX,{"derivedFrom":[subQ1,subQ0]});Q82=makeQuery(id+"F0.imprint","IMPRINT",FACE,{"disambiguationData":[TD([[makeQuery(id+"F0.imprint","IMPRINT",EDGE,{"disambiguationData":[TD([[subQ2,-1.0]])],"derivedFrom":subQ1}),1.0]])]});}
            var Q83;
            {var subQ0=sQuery(id+"F0.wireOp",EDGE,"E71.4.33");var subQ1=sQuery(id+"F0.wireOp",EDGE,"E71.4.0");var subQ2=makeQuery(id+"F0.imprint","INTERSECT",VERTEX,{"derivedFrom":[subQ1,subQ0]});Q83=makeQuery(id+"F0.imprint","IMPRINT",FACE,{"disambiguationData":[TD([[makeQuery(id+"F0.imprint","IMPRINT",EDGE,{"disambiguationData":[TD([[subQ2,-1.0]])],"derivedFrom":subQ1}),1.0]])]});}
            var Q84;
            {var subQ0=sQuery(id+"F0.wireOp",EDGE,"E71.3.33");var subQ1=sQuery(id+"F0.wireOp",EDGE,"E71.3.0");var subQ2=makeQuery(id+"F0.imprint","INTERSECT",VERTEX,{"derivedFrom":[subQ1,subQ0]});Q84=makeQuery(id+"F0.imprint","IMPRINT",FACE,{"disambiguationData":[TD([[makeQuery(id+"F0.imprint","IMPRINT",EDGE,{"disambiguationData":[TD([[subQ2,-1.0]])],"derivedFrom":subQ1}),1.0]])]});}
            var Q85;
            {var subQ3=sQuery(id+"F0.wireOp",EDGE,"E71.2.11");var subQ5=sQuery(id+"F0.wireOp",EDGE,"E71.3.11");var subQ6=makeQuery(id+"F0.imprint","INTERSECT",VERTEX,{"derivedFrom":[subQ3,subQ5]});Q85=makeQuery(id+"F0.imprint","IMPRINT",FACE,{"disambiguationData":[TD([[makeQuery(id+"F0.imprint","IMPRINT",EDGE,{"disambiguationData":[TD([[subQ6,-1.0]])],"derivedFrom":subQ3}),-1.0]])]});}
            var Q86;
            {var subQ0=sQuery(id+"F0.wireOp",EDGE,"E71.5.21");var subQ1=sQuery(id+"F0.wireOp",EDGE,"E71.1.11");var subQ2=makeQuery(id+"F0.imprint","INTERSECT",VERTEX,{"derivedFrom":[subQ1,subQ0]});Q86=makeQuery(id+"F0.imprint","IMPRINT",FACE,{"disambiguationData":[TD([[makeQuery(id+"F0.imprint","IMPRINT",EDGE,{"disambiguationData":[TD([[subQ2,1.0]])],"derivedFrom":subQ1}),-1.0]])]});}
            var Q87;
            {var subQ3=sQuery(id+"F0.wireOp",EDGE,"E71.1.11");var subQ5=sQuery(id+"F0.wireOp",EDGE,"E71.2.11");var subQ6=makeQuery(id+"F0.imprint","INTERSECT",VERTEX,{"derivedFrom":[subQ3,subQ5]});Q87=makeQuery(id+"F0.imprint","IMPRINT",FACE,{"disambiguationData":[TD([[makeQuery(id+"F0.imprint","IMPRINT",EDGE,{"disambiguationData":[TD([[subQ6,-1.0]])],"derivedFrom":subQ3}),-1.0]])]});}
            var Q88;
            {var subQ3=sQuery(id+"F0.wireOp",EDGE,"E71.4.11");var subQ5=sQuery(id+"F0.wireOp",EDGE,"E71.5.11");var subQ6=makeQuery(id+"F0.imprint","INTERSECT",VERTEX,{"derivedFrom":[subQ3,subQ5]});Q88=makeQuery(id+"F0.imprint","IMPRINT",FACE,{"disambiguationData":[TD([[makeQuery(id+"F0.imprint","IMPRINT",EDGE,{"disambiguationData":[TD([[subQ6,-1.0]])],"derivedFrom":subQ3}),-1.0]])]});}
            var Q89;
            {var subQ3=sQuery(id+"F0.wireOp",EDGE,"E71.5.11");var subQ5=sQuery(id+"F0.wireOp",EDGE,"E71.5.21");var subQ6=makeQuery(id+"F0.imprint","INTERSECT",VERTEX,{"derivedFrom":[subQ3,subQ5]});Q89=makeQuery(id+"F0.imprint","IMPRINT",FACE,{"disambiguationData":[TD([[makeQuery(id+"F0.imprint","IMPRINT",EDGE,{"disambiguationData":[TD([[subQ6,-1.0]])],"derivedFrom":subQ3}),-1.0]])]});}
            var Q90;
            {var subQ1=sQuery(id+"F0.wireOp",EDGE,"E6");var subQ3=sQuery(id+"F0.wireOp",EDGE,"E71.1.11");var subQ4=makeQuery(id+"F0.imprint","INTERSECT",VERTEX,{"derivedFrom":[subQ1,subQ3]});Q90=makeQuery(id+"F0.imprint","IMPRINT",FACE,{"disambiguationData":[TD([[makeQuery(id+"F0.imprint","IMPRINT",EDGE,{"disambiguationData":[TD([[subQ4,-1.0]])],"derivedFrom":subQ3}),-1.0]])]});}
            var Q91;
            {var subQ1=sQuery(id+"F0.wireOp",EDGE,"E71.3.10");var subQ3=sQuery(id+"F0.wireOp",EDGE,"E71.3.11");var subQ4=makeQuery(id+"F0.imprint","INTERSECT",VERTEX,{"derivedFrom":[subQ1,subQ3]});Q91=makeQuery(id+"F0.imprint","IMPRINT",FACE,{"disambiguationData":[TD([[makeQuery(id+"F0.imprint","IMPRINT",EDGE,{"disambiguationData":[TD([[subQ4,-1.0]])],"derivedFrom":subQ3}),-1.0]])]});}
            var Q92;
            {var subQ1=sQuery(id+"F0.wireOp",EDGE,"E67.MirrorCS");var subQ3=sQuery(id+"F0.wireOp",EDGE,"E71.5.21");var subQ4=makeQuery(id+"F0.imprint","INTERSECT",VERTEX,{"derivedFrom":[subQ1,subQ3]});Q92=makeQuery(id+"F0.imprint","IMPRINT",FACE,{"disambiguationData":[TD([[makeQuery(id+"F0.imprint","IMPRINT",EDGE,{"disambiguationData":[TD([[subQ4,-1.0]])],"derivedFrom":subQ3}),1.0]])]});}
            var Q93;
            {var subQ1=sQuery(id+"F0.wireOp",EDGE,"E71.5.10");var subQ3=sQuery(id+"F0.wireOp",EDGE,"E71.5.11");var subQ4=makeQuery(id+"F0.imprint","INTERSECT",VERTEX,{"derivedFrom":[subQ1,subQ3]});Q93=makeQuery(id+"F0.imprint","IMPRINT",FACE,{"disambiguationData":[TD([[makeQuery(id+"F0.imprint","IMPRINT",EDGE,{"disambiguationData":[TD([[subQ4,-1.0]])],"derivedFrom":subQ3}),-1.0]])]});}
            var Q94;
            {var subQ1=sQuery(id+"F0.wireOp",EDGE,"E71.4.10");var subQ3=sQuery(id+"F0.wireOp",EDGE,"E71.4.11");var subQ4=makeQuery(id+"F0.imprint","INTERSECT",VERTEX,{"derivedFrom":[subQ1,subQ3]});Q94=makeQuery(id+"F0.imprint","IMPRINT",FACE,{"disambiguationData":[TD([[makeQuery(id+"F0.imprint","IMPRINT",EDGE,{"disambiguationData":[TD([[subQ4,-1.0]])],"derivedFrom":subQ3}),-1.0]])]});}
            var Q95;
            {var subQ1=sQuery(id+"F0.wireOp",EDGE,"E71.2.10");var subQ3=sQuery(id+"F0.wireOp",EDGE,"E71.2.11");var subQ4=makeQuery(id+"F0.imprint","INTERSECT",VERTEX,{"derivedFrom":[subQ1,subQ3]});Q95=makeQuery(id+"F0.imprint","IMPRINT",FACE,{"disambiguationData":[TD([[makeQuery(id+"F0.imprint","IMPRINT",EDGE,{"disambiguationData":[TD([[subQ4,-1.0]])],"derivedFrom":subQ3}),-1.0]])]});}
            extrude(context, id + "F1", {"entities" : qUnion([Q0, Q1, Q2, Q3, Q4, Q5, Q6, Q7, Q8, Q9, Q10, Q11, Q12, Q13, Q14, Q15, Q16, Q17, Q18, Q19, Q20, Q21, Q22, Q23, Q24, Q25, Q26, Q27, Q28, Q29, Q30, Q31, Q32, Q33, Q34, Q35, Q36, Q37, Q38, Q39, Q40, Q41, Q42, Q43, Q44, Q45, Q46, Q47, Q48, Q49, Q50, Q51, Q52, Q53, Q54, Q55, Q56, Q57, Q58, Q59, Q60, Q61, Q62, Q63, Q64, Q65, Q66, Q67, Q68, Q69, Q70, Q71, Q72, Q73, Q74, Q75, Q76, Q77, Q78, Q79, Q80, Q81, Q82, Q83, Q84, Q85, Q86, Q87, Q88, Q89, Q90, Q91, Q92, Q93, Q94, Q95]), "depth" : 1.5 * mm});
        }
        {
            var Q0;
            Q0=makeQuery(id+"F1.opExtrude","SWEPT_BODY",BODY,{"disambiguationData":[OSD([sQuery(id+"F0.wireOp",EDGE,"E8"),sQuery(id+"F0.wireOp",EDGE,"E9"),sQuery(id+"F0.wireOp",EDGE,"E10"),sQuery(id+"F0.wireOp",EDGE,"E11"),sQuery(id+"F0.wireOp",EDGE,"E12"),sQuery(id+"F0.wireOp",EDGE,"E13"),sQuery(id+"F0.wireOp",EDGE,"E14"),sQuery(id+"F0.wireOp",EDGE,"E15"),sQuery(id+"F0.wireOp",EDGE,"E16"),sQuery(id+"F0.wireOp",EDGE,"E20"),sQuery(id+"F0.wireOp",EDGE,"E21"),sQuery(id+"F0.wireOp",EDGE,"E22"),sQuery(id+"F0.wireOp",EDGE,"E23"),sQuery(id+"F0.wireOp",EDGE,"E26"),sQuery(id+"F0.wireOp",EDGE,"E27"),sQuery(id+"F0.wireOp",EDGE,"E28"),sQuery(id+"F0.wireOp",EDGE,"E29"),sQuery(id+"F0.wireOp",EDGE,"E33"),sQuery(id+"F0.wireOp",EDGE,"E34"),sQuery(id+"F0.wireOp",EDGE,"E35"),sQuery(id+"F0.wireOp",EDGE,"E39.MirrorCS"),sQuery(id+"F0.wireOp",EDGE,"E40.MirrorCS"),sQuery(id+"F0.wireOp",EDGE,"E41.MirrorCS"),sQuery(id+"F0.wireOp",EDGE,"E43.MirrorCS"),sQuery(id+"F0.wireOp",EDGE,"E44.MirrorCS"),sQuery(id+"F0.wireOp",EDGE,"E47.MirrorCS"),sQuery(id+"F0.wireOp",EDGE,"E49.MirrorCS"),sQuery(id+"F0.wireOp",EDGE,"E50.MirrorCS"),sQuery(id+"F0.wireOp",EDGE,"E51.MirrorCS"),sQuery(id+"F0.wireOp",EDGE,"E52.MirrorCS"),sQuery(id+"F0.wireOp",EDGE,"E53.MirrorCS"),sQuery(id+"F0.wireOp",EDGE,"E54.MirrorCS"),sQuery(id+"F0.wireOp",EDGE,"E55.MirrorCS"),sQuery(id+"F0.wireOp",EDGE,"E57.MirrorCS"),sQuery(id+"F0.wireOp",EDGE,"E58.MirrorCS"),sQuery(id+"F0.wireOp",EDGE,"E60.MirrorCS"),sQuery(id+"F0.wireOp",EDGE,"E61.MirrorCS"),sQuery(id+"F0.wireOp",EDGE,"E62.MirrorCS"),sQuery(id+"F0.wireOp",EDGE,"E66.MirrorCS"),sQuery(id+"F0.wireOp",EDGE,"E69.MirrorCS"),sQuery(id+"F0.wireOp",EDGE,"E71.1.0"),sQuery(id+"F0.wireOp",EDGE,"E71.1.1"),sQuery(id+"F0.wireOp",EDGE,"E71.1.2"),sQuery(id+"F0.wireOp",EDGE,"E71.1.3"),sQuery(id+"F0.wireOp",EDGE,"E71.1.4"),sQuery(id+"F0.wireOp",EDGE,"E71.1.7"),sQuery(id+"F0.wireOp",EDGE,"E71.1.9"),sQuery(id+"F0.wireOp",EDGE,"E6"),sQuery(id+"F0.wireOp",EDGE,"E71.1.11"),sQuery(id+"F0.wireOp",EDGE,"E71.1.13"),sQuery(id+"F0.wireOp",EDGE,"E71.1.14"),sQuery(id+"F0.wireOp",EDGE,"E71.1.16"),sQuery(id+"F0.wireOp",EDGE,"E71.1.22"),sQuery(id+"F0.wireOp",EDGE,"E71.1.23"),sQuery(id+"F0.wireOp",EDGE,"E71.1.24"),sQuery(id+"F0.wireOp",EDGE,"E71.1.25"),sQuery(id+"F0.wireOp",EDGE,"E71.1.26"),sQuery(id+"F0.wireOp",EDGE,"E71.1.27"),sQuery(id+"F0.wireOp",EDGE,"E71.1.29"),sQuery(id+"F0.wireOp",EDGE,"E71.1.30"),sQuery(id+"F0.wireOp",EDGE,"E71.1.31"),sQuery(id+"F0.wireOp",EDGE,"E71.1.32"),sQuery(id+"F0.wireOp",EDGE,"E5"),sQuery(id+"F0.wireOp",EDGE,"E71.1.34"),sQuery(id+"F0.wireOp",EDGE,"E71.1.35"),sQuery(id+"F0.wireOp",EDGE,"E71.1.36"),sQuery(id+"F0.wireOp",EDGE,"E71.1.37"),sQuery(id+"F0.wireOp",EDGE,"E71.1.38"),sQuery(id+"F0.wireOp",EDGE,"E71.1.39"),sQuery(id+"F0.wireOp",EDGE,"E71.1.40"),sQuery(id+"F0.wireOp",EDGE,"E71.1.41"),sQuery(id+"F0.wireOp",EDGE,"E71.1.42"),sQuery(id+"F0.wireOp",EDGE,"E71.1.45"),sQuery(id+"F0.wireOp",EDGE,"E71.1.46"),sQuery(id+"F0.wireOp",EDGE,"E71.1.48"),sQuery(id+"F0.wireOp",EDGE,"E71.1.51"),sQuery(id+"F0.wireOp",EDGE,"E71.1.52"),sQuery(id+"F0.wireOp",EDGE,"E71.1.53"),sQuery(id+"F0.wireOp",EDGE,"E71.1.54"),sQuery(id+"F0.wireOp",EDGE,"E71.1.55"),sQuery(id+"F0.wireOp",EDGE,"E71.1.59"),sQuery(id+"F0.wireOp",EDGE,"E71.1.61"),sQuery(id+"F0.wireOp",EDGE,"E71.1.62"),sQuery(id+"F0.wireOp",EDGE,"E71.1.63"),sQuery(id+"F0.wireOp",EDGE,"E71.1.65"),sQuery(id+"F0.wireOp",EDGE,"E71.2.0"),sQuery(id+"F0.wireOp",EDGE,"E71.2.1"),sQuery(id+"F0.wireOp",EDGE,"E71.2.2"),sQuery(id+"F0.wireOp",EDGE,"E71.2.3"),sQuery(id+"F0.wireOp",EDGE,"E71.2.4"),sQuery(id+"F0.wireOp",EDGE,"E71.2.7"),sQuery(id+"F0.wireOp",EDGE,"E71.2.9"),sQuery(id+"F0.wireOp",EDGE,"E71.2.10"),sQuery(id+"F0.wireOp",EDGE,"E71.2.11"),sQuery(id+"F0.wireOp",EDGE,"E71.2.13"),sQuery(id+"F0.wireOp",EDGE,"E71.2.14"),sQuery(id+"F0.wireOp",EDGE,"E71.2.16"),sQuery(id+"F0.wireOp",EDGE,"E71.2.22"),sQuery(id+"F0.wireOp",EDGE,"E71.2.23"),sQuery(id+"F0.wireOp",EDGE,"E71.2.24"),sQuery(id+"F0.wireOp",EDGE,"E71.2.25"),sQuery(id+"F0.wireOp",EDGE,"E71.2.26"),sQuery(id+"F0.wireOp",EDGE,"E71.2.27"),sQuery(id+"F0.wireOp",EDGE,"E71.2.29"),sQuery(id+"F0.wireOp",EDGE,"E71.2.30"),sQuery(id+"F0.wireOp",EDGE,"E71.2.31"),sQuery(id+"F0.wireOp",EDGE,"E71.2.32"),sQuery(id+"F0.wireOp",EDGE,"E71.2.33"),sQuery(id+"F0.wireOp",EDGE,"E71.2.34"),sQuery(id+"F0.wireOp",EDGE,"E71.2.35"),sQuery(id+"F0.wireOp",EDGE,"E71.2.36"),sQuery(id+"F0.wireOp",EDGE,"E71.2.37"),sQuery(id+"F0.wireOp",EDGE,"E71.2.38"),sQuery(id+"F0.wireOp",EDGE,"E71.2.39"),sQuery(id+"F0.wireOp",EDGE,"E71.2.40"),sQuery(id+"F0.wireOp",EDGE,"E71.2.41"),sQuery(id+"F0.wireOp",EDGE,"E71.2.42"),sQuery(id+"F0.wireOp",EDGE,"E71.2.45"),sQuery(id+"F0.wireOp",EDGE,"E71.2.46"),sQuery(id+"F0.wireOp",EDGE,"E71.2.48"),sQuery(id+"F0.wireOp",EDGE,"E71.2.51"),sQuery(id+"F0.wireOp",EDGE,"E71.2.52"),sQuery(id+"F0.wireOp",EDGE,"E71.2.53"),sQuery(id+"F0.wireOp",EDGE,"E71.2.54"),sQuery(id+"F0.wireOp",EDGE,"E71.2.55"),sQuery(id+"F0.wireOp",EDGE,"E71.2.59"),sQuery(id+"F0.wireOp",EDGE,"E71.2.61"),sQuery(id+"F0.wireOp",EDGE,"E71.2.62"),sQuery(id+"F0.wireOp",EDGE,"E71.2.63"),sQuery(id+"F0.wireOp",EDGE,"E71.2.65"),sQuery(id+"F0.wireOp",EDGE,"E71.3.0"),sQuery(id+"F0.wireOp",EDGE,"E71.3.1"),sQuery(id+"F0.wireOp",EDGE,"E71.3.2"),sQuery(id+"F0.wireOp",EDGE,"E71.3.3"),sQuery(id+"F0.wireOp",EDGE,"E71.3.4"),sQuery(id+"F0.wireOp",EDGE,"E71.3.7"),sQuery(id+"F0.wireOp",EDGE,"E71.3.9"),sQuery(id+"F0.wireOp",EDGE,"E71.3.10"),sQuery(id+"F0.wireOp",EDGE,"E71.3.11"),sQuery(id+"F0.wireOp",EDGE,"E71.3.13"),sQuery(id+"F0.wireOp",EDGE,"E71.3.14"),sQuery(id+"F0.wireOp",EDGE,"E71.3.16"),sQuery(id+"F0.wireOp",EDGE,"E71.3.22"),sQuery(id+"F0.wireOp",EDGE,"E71.3.23"),sQuery(id+"F0.wireOp",EDGE,"E71.3.24"),sQuery(id+"F0.wireOp",EDGE,"E71.3.25"),sQuery(id+"F0.wireOp",EDGE,"E71.3.26"),sQuery(id+"F0.wireOp",EDGE,"E71.3.27"),sQuery(id+"F0.wireOp",EDGE,"E71.3.29"),sQuery(id+"F0.wireOp",EDGE,"E71.3.30"),sQuery(id+"F0.wireOp",EDGE,"E71.3.31"),sQuery(id+"F0.wireOp",EDGE,"E71.3.32"),sQuery(id+"F0.wireOp",EDGE,"E71.3.33"),sQuery(id+"F0.wireOp",EDGE,"E71.3.34"),sQuery(id+"F0.wireOp",EDGE,"E71.3.35"),sQuery(id+"F0.wireOp",EDGE,"E71.3.36"),sQuery(id+"F0.wireOp",EDGE,"E71.3.37"),sQuery(id+"F0.wireOp",EDGE,"E71.3.38"),sQuery(id+"F0.wireOp",EDGE,"E71.3.39"),sQuery(id+"F0.wireOp",EDGE,"E71.3.40"),sQuery(id+"F0.wireOp",EDGE,"E71.3.41"),sQuery(id+"F0.wireOp",EDGE,"E71.3.42"),sQuery(id+"F0.wireOp",EDGE,"E71.3.45"),sQuery(id+"F0.wireOp",EDGE,"E71.3.46"),sQuery(id+"F0.wireOp",EDGE,"E71.3.48"),sQuery(id+"F0.wireOp",EDGE,"E71.3.51"),sQuery(id+"F0.wireOp",EDGE,"E71.3.52"),sQuery(id+"F0.wireOp",EDGE,"E71.3.53"),sQuery(id+"F0.wireOp",EDGE,"E71.3.54"),sQuery(id+"F0.wireOp",EDGE,"E71.3.55"),sQuery(id+"F0.wireOp",EDGE,"E71.3.59"),sQuery(id+"F0.wireOp",EDGE,"E71.3.61"),sQuery(id+"F0.wireOp",EDGE,"E71.3.62"),sQuery(id+"F0.wireOp",EDGE,"E71.3.63"),sQuery(id+"F0.wireOp",EDGE,"E71.3.65"),sQuery(id+"F0.wireOp",EDGE,"E71.4.0"),sQuery(id+"F0.wireOp",EDGE,"E71.4.1"),sQuery(id+"F0.wireOp",EDGE,"E71.4.2"),sQuery(id+"F0.wireOp",EDGE,"E71.4.3"),sQuery(id+"F0.wireOp",EDGE,"E71.4.4"),sQuery(id+"F0.wireOp",EDGE,"E71.4.7"),sQuery(id+"F0.wireOp",EDGE,"E71.4.9"),sQuery(id+"F0.wireOp",EDGE,"E71.4.10"),sQuery(id+"F0.wireOp",EDGE,"E71.4.11"),sQuery(id+"F0.wireOp",EDGE,"E71.4.13"),sQuery(id+"F0.wireOp",EDGE,"E71.4.14"),sQuery(id+"F0.wireOp",EDGE,"E71.4.16"),sQuery(id+"F0.wireOp",EDGE,"E71.4.22"),sQuery(id+"F0.wireOp",EDGE,"E71.4.23"),sQuery(id+"F0.wireOp",EDGE,"E71.4.24"),sQuery(id+"F0.wireOp",EDGE,"E71.4.25"),sQuery(id+"F0.wireOp",EDGE,"E71.4.26"),sQuery(id+"F0.wireOp",EDGE,"E71.4.27"),sQuery(id+"F0.wireOp",EDGE,"E71.4.29"),sQuery(id+"F0.wireOp",EDGE,"E71.4.30"),sQuery(id+"F0.wireOp",EDGE,"E71.4.31"),sQuery(id+"F0.wireOp",EDGE,"E71.4.32"),sQuery(id+"F0.wireOp",EDGE,"E71.4.33"),sQuery(id+"F0.wireOp",EDGE,"E71.4.34"),sQuery(id+"F0.wireOp",EDGE,"E71.4.35"),sQuery(id+"F0.wireOp",EDGE,"E71.4.36"),sQuery(id+"F0.wireOp",EDGE,"E71.4.37"),sQuery(id+"F0.wireOp",EDGE,"E71.4.38"),sQuery(id+"F0.wireOp",EDGE,"E71.4.39"),sQuery(id+"F0.wireOp",EDGE,"E71.4.40"),sQuery(id+"F0.wireOp",EDGE,"E71.4.41"),sQuery(id+"F0.wireOp",EDGE,"E71.4.42"),sQuery(id+"F0.wireOp",EDGE,"E71.4.45"),sQuery(id+"F0.wireOp",EDGE,"E71.4.46"),sQuery(id+"F0.wireOp",EDGE,"E71.4.48"),sQuery(id+"F0.wireOp",EDGE,"E71.4.51"),sQuery(id+"F0.wireOp",EDGE,"E71.4.52"),sQuery(id+"F0.wireOp",EDGE,"E71.4.53"),sQuery(id+"F0.wireOp",EDGE,"E71.4.54"),sQuery(id+"F0.wireOp",EDGE,"E71.4.55"),sQuery(id+"F0.wireOp",EDGE,"E71.4.59"),sQuery(id+"F0.wireOp",EDGE,"E71.4.61"),sQuery(id+"F0.wireOp",EDGE,"E71.4.62"),sQuery(id+"F0.wireOp",EDGE,"E71.4.63"),sQuery(id+"F0.wireOp",EDGE,"E71.4.65"),sQuery(id+"F0.wireOp",EDGE,"E71.5.0"),sQuery(id+"F0.wireOp",EDGE,"E71.5.1"),sQuery(id+"F0.wireOp",EDGE,"E71.5.2"),sQuery(id+"F0.wireOp",EDGE,"E71.5.3"),sQuery(id+"F0.wireOp",EDGE,"E71.5.4"),sQuery(id+"F0.wireOp",EDGE,"E71.5.7"),sQuery(id+"F0.wireOp",EDGE,"E71.5.8"),sQuery(id+"F0.wireOp",EDGE,"E71.5.9"),sQuery(id+"F0.wireOp",EDGE,"E71.5.10"),sQuery(id+"F0.wireOp",EDGE,"E71.5.11"),sQuery(id+"F0.wireOp",EDGE,"E71.5.13"),sQuery(id+"F0.wireOp",EDGE,"E71.5.14"),sQuery(id+"F0.wireOp",EDGE,"E71.5.16"),sQuery(id+"F0.wireOp",EDGE,"E71.5.17"),sQuery(id+"F0.wireOp",EDGE,"E67.MirrorCS"),sQuery(id+"F0.wireOp",EDGE,"E68.MirrorCS"),sQuery(id+"F0.wireOp",EDGE,"E71.5.21"),sQuery(id+"F0.wireOp",EDGE,"E71.5.22"),sQuery(id+"F0.wireOp",EDGE,"E71.5.23"),sQuery(id+"F0.wireOp",EDGE,"E71.5.24"),sQuery(id+"F0.wireOp",EDGE,"E71.5.25"),sQuery(id+"F0.wireOp",EDGE,"E71.5.26"),sQuery(id+"F0.wireOp",EDGE,"E71.5.27"),sQuery(id+"F0.wireOp",EDGE,"E71.5.29"),sQuery(id+"F0.wireOp",EDGE,"E71.5.30"),sQuery(id+"F0.wireOp",EDGE,"E71.5.31"),sQuery(id+"F0.wireOp",EDGE,"E71.5.32"),sQuery(id+"F0.wireOp",EDGE,"E71.5.33"),sQuery(id+"F0.wireOp",EDGE,"E71.5.34"),sQuery(id+"F0.wireOp",EDGE,"E71.5.35"),sQuery(id+"F0.wireOp",EDGE,"E71.5.36"),sQuery(id+"F0.wireOp",EDGE,"E71.5.37"),sQuery(id+"F0.wireOp",EDGE,"E71.5.38"),sQuery(id+"F0.wireOp",EDGE,"E71.5.39"),sQuery(id+"F0.wireOp",EDGE,"E71.5.40"),sQuery(id+"F0.wireOp",EDGE,"E71.5.41"),sQuery(id+"F0.wireOp",EDGE,"E71.5.42"),sQuery(id+"F0.wireOp",EDGE,"E71.5.45"),sQuery(id+"F0.wireOp",EDGE,"E71.5.46"),sQuery(id+"F0.wireOp",EDGE,"E71.5.48"),sQuery(id+"F0.wireOp",EDGE,"E71.5.51"),sQuery(id+"F0.wireOp",EDGE,"E71.5.52"),sQuery(id+"F0.wireOp",EDGE,"E71.5.53"),sQuery(id+"F0.wireOp",EDGE,"E71.5.54"),sQuery(id+"F0.wireOp",EDGE,"E71.5.55"),sQuery(id+"F0.wireOp",EDGE,"E71.5.59"),sQuery(id+"F0.wireOp",EDGE,"E71.5.61"),sQuery(id+"F0.wireOp",EDGE,"E71.5.62"),sQuery(id+"F0.wireOp",EDGE,"E71.5.63"),sQuery(id+"F0.wireOp",EDGE,"E71.5.65")])]});
            var Q1;
            Q1=qCreatedBy(makeId("Origin.pointOp"),VERTEX);
            transform(context, id + "F2", {"entities" : qUnion([Q0]), "transformType" : TransformType.SCALE_UNIFORMLY, "scale" : 2, "scalePoint" : qUnion([Q1]), "makeCopy" : false});
        }
    });
